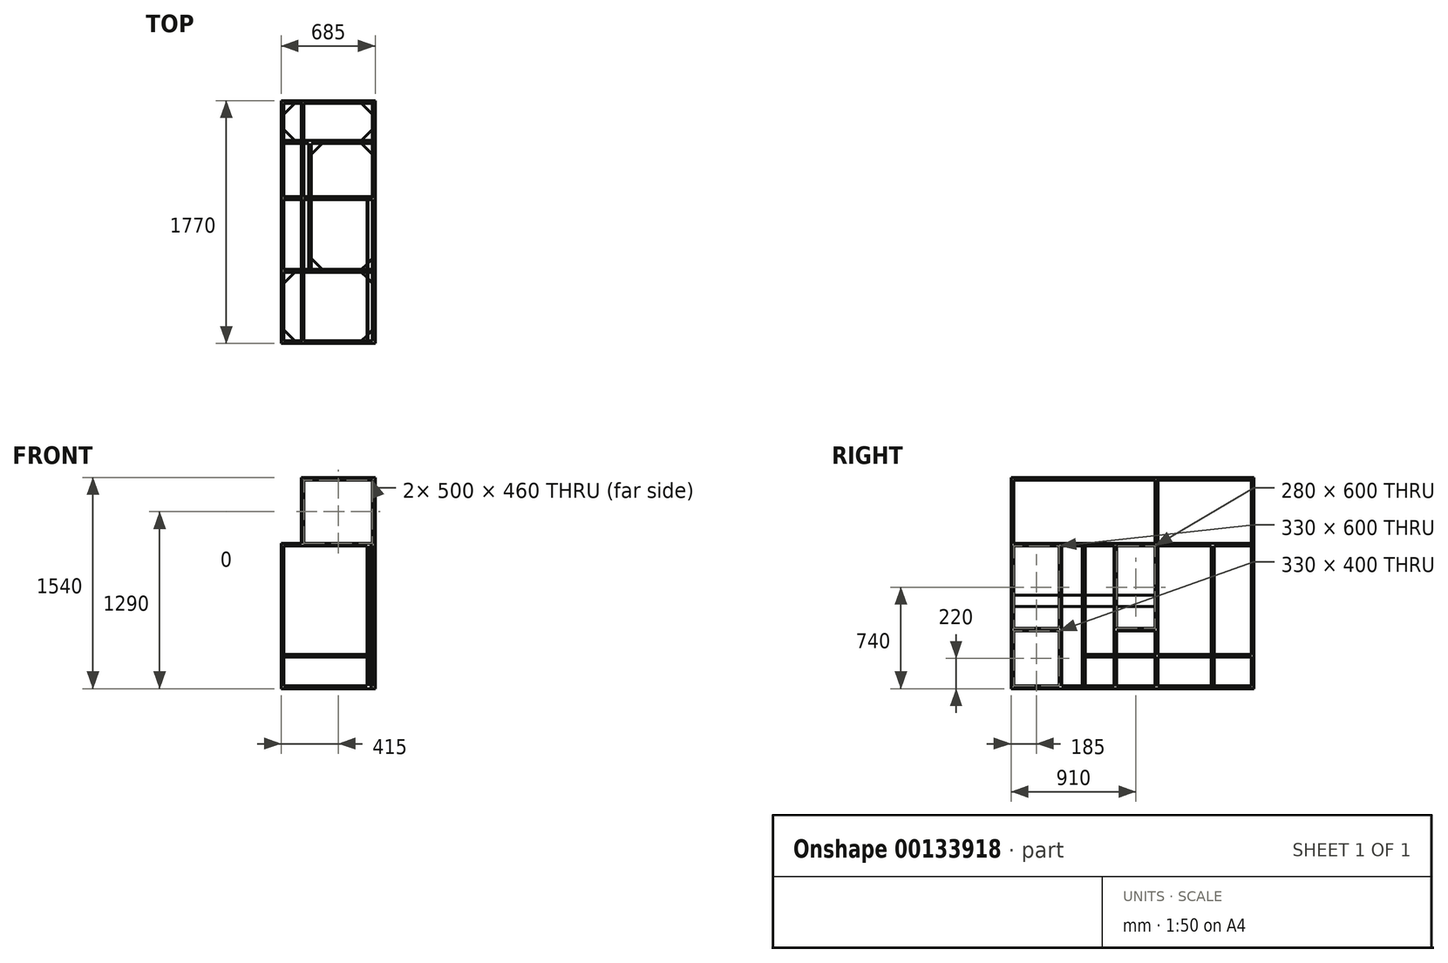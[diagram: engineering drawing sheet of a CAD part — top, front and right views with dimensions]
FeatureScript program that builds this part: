
annotation { "Feature Type Name" : "Feature", "Feature Type Description" : "" }
export const myFeature = defineFeature(function(context is Context, id is Id, definition is map)
    precondition{}
    {
        {
            var Q0;
            Q0=qCreatedBy(makeId("Front.planeOp"),FACE);
            var sketch = newSketch(context, id + "F0", { "sketchPlane" : qUnion([Q0])});
            skLineSegment(sketch, "E0.bottom", {"start": v(0, 0) * mm, "end": v(20, 0) * mm});
            skLineSegment(sketch, "E0.top", {"start": v(0, 20) * mm, "end": v(20, 20) * mm});
            skLineSegment(sketch, "E0.left", {"start": v(0, 0) * mm, "end": v(0, 20) * mm});
            skLineSegment(sketch, "E0.right", {"start": v(20, 0) * mm, "end": v(20, 20) * mm});
            skSolve(sketch);
        }
        {
            var Q0;
            Q0 = qSketchRegion(id + "F0", true);
            extrude(context, id + "F1", {"entities" : qUnion([Q0]), "oppositeDirection" : true, "depth" : 1770 * mm});
        }
        {
            var Q0;
            Q0=makeQuery(id+"F1.opExtrude","SWEPT_FACE",FACE,{"disambiguationData":[OSD([sQuery(id+"F0.wireOp",EDGE,"E0.left")])]});
            var sketch = newSketch(context, id + "F2", { "sketchPlane" : qUnion([Q0])});
            skLineSegment(sketch, "E1.bottom", {"start": v(0, 20) * mm, "end": v(-20, 20) * mm});
            skLineSegment(sketch, "E1.top", {"start": v(0, 0) * mm, "end": v(-20, 0) * mm});
            skLineSegment(sketch, "E1.left", {"start": v(0, 20) * mm, "end": v(0, 0) * mm});
            skLineSegment(sketch, "E1.right", {"start": v(-20, 20) * mm, "end": v(-20, 0) * mm});
            skLineSegment(sketch, "E2.bottom", {"start": v(-1770, 20) * mm, "end": v(-1750, 20) * mm});
            skLineSegment(sketch, "E2.top", {"start": v(-1770, 0) * mm, "end": v(-1750, 0) * mm});
            skLineSegment(sketch, "E2.left", {"start": v(-1770, 20) * mm, "end": v(-1770, 0) * mm});
            skLineSegment(sketch, "E2.right", {"start": v(-1750, 20) * mm, "end": v(-1750, 0) * mm});
            skSolve(sketch);
        }
        {
            var Q0;
            Q0 = qSketchRegion(id + "F2", true);
            extrude(context, id + "F3", {"entities" : qUnion([Q0]), "operationType" : NewBodyOperationType.ADD, "depth" : 665 * mm});
        }
        {
            var Q0;
            Q0=makeQuery(id+"F3.opExtrude","SWEPT_FACE",FACE,{"disambiguationData":[OSD([sQuery(id+"F2.wireOp",EDGE,"E1.right")])]});
            var sketch = newSketch(context, id + "F4", { "sketchPlane" : qUnion([Q0])});
            skLineSegment(sketch, "E3.bottom", {"start": v(665, 20) * mm, "end": v(645, 20) * mm});
            skLineSegment(sketch, "E3.top", {"start": v(665, 0) * mm, "end": v(645, 0) * mm});
            skLineSegment(sketch, "E3.left", {"start": v(665, 20) * mm, "end": v(665, 0) * mm});
            skLineSegment(sketch, "E3.right", {"start": v(645, 20) * mm, "end": v(645, 0) * mm});
            skSolve(sketch);
        }
        {
            var Q0;
            Q0 = qSketchRegion(id + "F4", true);
            extrude(context, id + "F5", {"entities" : qUnion([Q0]), "operationType" : NewBodyOperationType.ADD, "depth" : 520 * mm});
        }
        {
            var Q0;
            Q0=makeQuery(id+"F3.opExtrude","SWEPT_FACE",FACE,{"disambiguationData":[OSD([sQuery(id+"F2.wireOp",EDGE,"E2.right")])]});
            var sketch = newSketch(context, id + "F6", { "sketchPlane" : qUnion([Q0])});
            skLineSegment(sketch, "E4.bottom", {"start": v(-665, 20) * mm, "end": v(-645, 20) * mm});
            skLineSegment(sketch, "E4.top", {"start": v(-665, 0) * mm, "end": v(-645, 0) * mm});
            skLineSegment(sketch, "E4.left", {"start": v(-665, 20) * mm, "end": v(-665, 0) * mm});
            skLineSegment(sketch, "E4.right", {"start": v(-645, 20) * mm, "end": v(-645, 0) * mm});
            skSolve(sketch);
        }
        {
            var Q0;
            Q0 = qSketchRegion(id + "F6", true);
            extrude(context, id + "F7", {"entities" : qUnion([Q0]), "operationType" : NewBodyOperationType.ADD, "depth" : 290 * mm});
        }
        {
            var Q0;
            Q0=makeQuery(id+"F5.opExtrude","SWEPT_FACE",FACE,{"disambiguationData":[OSD([sQuery(id+"F4.wireOp",EDGE,"E3.right")])]});
            var sketch = newSketch(context, id + "F8", { "sketchPlane" : qUnion([Q0])});
            skLineSegment(sketch, "E5.bottom", {"start": v(540, 20) * mm, "end": v(520, 20) * mm});
            skLineSegment(sketch, "E5.top", {"start": v(540, 0) * mm, "end": v(520, 0) * mm});
            skLineSegment(sketch, "E5.left", {"start": v(540, 20) * mm, "end": v(540, 0) * mm});
            skLineSegment(sketch, "E5.right", {"start": v(520, 20) * mm, "end": v(520, 0) * mm});
            skSolve(sketch);
        }
        {
            var Q0;
            Q0 = qSketchRegion(id + "F8", true);
            extrude(context, id + "F9", {"entities" : qUnion([Q0]), "operationType" : NewBodyOperationType.ADD, "endBound" : BoundingType.UP_TO_NEXT, "depth" : 25 * mm});
        }
        {
            var Q0;
            Q0=makeQuery(id+"F7.opExtrude","SWEPT_FACE",FACE,{"disambiguationData":[OSD([sQuery(id+"F6.wireOp",EDGE,"E4.right")])]});
            var sketch = newSketch(context, id + "F10", { "sketchPlane" : qUnion([Q0])});
            skLineSegment(sketch, "E6.bottom", {"start": v(1460, 20) * mm, "end": v(1480, 20) * mm});
            skLineSegment(sketch, "E6.top", {"start": v(1460, 0) * mm, "end": v(1480, 0) * mm});
            skLineSegment(sketch, "E6.left", {"start": v(1460, 20) * mm, "end": v(1460, 0) * mm});
            skLineSegment(sketch, "E6.right", {"start": v(1480, 20) * mm, "end": v(1480, 0) * mm});
            skSolve(sketch);
        }
        {
            var Q0;
            Q0 = qSketchRegion(id + "F10", true);
            extrude(context, id + "F11", {"entities" : qUnion([Q0]), "operationType" : NewBodyOperationType.ADD, "endBound" : BoundingType.UP_TO_NEXT, "depth" : 25 * mm});
        }
        {
            var Q0;
            Q0=makeQuery(id+"F11.boolean.opBoolean","MERGE",FACE,{"derivedFrom":[makeQuery(id+"F7.opExtrude","CAP_FACE",FACE,{"disambiguationData":[OSD([sQuery(id+"F6.wireOp",EDGE,"E4.bottom"),sQuery(id+"F6.wireOp",EDGE,"E4.top"),sQuery(id+"F6.wireOp",EDGE,"E4.left"),sQuery(id+"F6.wireOp",EDGE,"E4.right")])],"isStart":false}),makeQuery(id+"F11.opExtrude","SWEPT_FACE",FACE,{"disambiguationData":[OSD([sQuery(id+"F10.wireOp",EDGE,"E6.left")])]})]});
            var sketch = newSketch(context, id + "F12", { "sketchPlane" : qUnion([Q0])});
            skLineSegment(sketch, "E7.bottom", {"start": v(-465, 20) * mm, "end": v(-445, 20) * mm});
            skLineSegment(sketch, "E7.top", {"start": v(-465, 0) * mm, "end": v(-445, 0) * mm});
            skLineSegment(sketch, "E7.left", {"start": v(-465, 20) * mm, "end": v(-465, 0) * mm});
            skLineSegment(sketch, "E7.right", {"start": v(-445, 20) * mm, "end": v(-445, 0) * mm});
            skSolve(sketch);
        }
        {
            var Q0;
            Q0 = qSketchRegion(id + "F12", true);
            extrude(context, id + "F13", {"entities" : qUnion([Q0]), "operationType" : NewBodyOperationType.ADD, "endBound" : BoundingType.UP_TO_NEXT, "depth" : 25 * mm});
        }
        {
            var Q0;
            Q0=makeQuery(id+"F13.boolean.opBoolean","MERGE",FACE,{"derivedFrom":[makeQuery(id+"F11.boolean.opBoolean","MERGE",FACE,{"derivedFrom":[makeQuery(id+"F9.boolean.opBoolean","MERGE",FACE,{"derivedFrom":[makeQuery(id+"F7.boolean.opBoolean","MERGE",FACE,{"derivedFrom":[makeQuery(id+"F5.boolean.opBoolean","MERGE",FACE,{"derivedFrom":[makeQuery(id+"F3.boolean.opBoolean","MERGE",FACE,{"derivedFrom":[makeQuery(id+"F1.opExtrude","SWEPT_FACE",FACE,{"disambiguationData":[OSD([sQuery(id+"F0.wireOp",EDGE,"E0.top")])]}),makeQuery(id+"F3.opExtrude","SWEPT_FACE",FACE,{"disambiguationData":[OSD([sQuery(id+"F2.wireOp",EDGE,"E1.bottom")])]}),makeQuery(id+"F3.opExtrude","SWEPT_FACE",FACE,{"disambiguationData":[OSD([sQuery(id+"F2.wireOp",EDGE,"E2.bottom")])]})]}),makeQuery(id+"F5.opExtrude","SWEPT_FACE",FACE,{"disambiguationData":[OSD([sQuery(id+"F4.wireOp",EDGE,"E3.bottom")])]})]}),makeQuery(id+"F7.opExtrude","SWEPT_FACE",FACE,{"disambiguationData":[OSD([sQuery(id+"F6.wireOp",EDGE,"E4.bottom")])]})]}),makeQuery(id+"F9.opExtrude","SWEPT_FACE",FACE,{"disambiguationData":[OSD([sQuery(id+"F8.wireOp",EDGE,"E5.bottom")])]})]}),makeQuery(id+"F11.opExtrude","SWEPT_FACE",FACE,{"disambiguationData":[OSD([sQuery(id+"F10.wireOp",EDGE,"E6.bottom")])]})]}),makeQuery(id+"F13.opExtrude","SWEPT_FACE",FACE,{"disambiguationData":[OSD([sQuery(id+"F12.wireOp",EDGE,"E7.bottom")])]})]});
            var sketch = newSketch(context, id + "F14", { "sketchPlane" : qUnion([Q0])});
            skLineSegment(sketch, "E8.bottom", {"start": v(0, 20) * mm, "end": v(20, 20) * mm});
            skLineSegment(sketch, "E8.top", {"start": v(0, 0) * mm, "end": v(20, 0) * mm});
            skLineSegment(sketch, "E8.left", {"start": v(0, 20) * mm, "end": v(0, 0) * mm});
            skLineSegment(sketch, "E8.right", {"start": v(20, 20) * mm, "end": v(20, 0) * mm});
            skLineSegment(sketch, "E9.bottom", {"start": v(-665, 0) * mm, "end": v(-645, 0) * mm});
            skLineSegment(sketch, "E9.top", {"start": v(-665, 20) * mm, "end": v(-645, 20) * mm});
            skLineSegment(sketch, "E9.left", {"start": v(-665, 0) * mm, "end": v(-665, 20) * mm});
            skLineSegment(sketch, "E9.right", {"start": v(-645, 0) * mm, "end": v(-645, 20) * mm});
            skLineSegment(sketch, "E10.bottom", {"start": v(-645, 520) * mm, "end": v(-665, 520) * mm});
            skLineSegment(sketch, "E10.top", {"start": v(-645, 540) * mm, "end": v(-665, 540) * mm});
            skLineSegment(sketch, "E10.left", {"start": v(-645, 520) * mm, "end": v(-645, 540) * mm});
            skLineSegment(sketch, "E10.right", {"start": v(-665, 520) * mm, "end": v(-665, 540) * mm});
            skLineSegment(sketch, "E11.bottom", {"start": v(20, 1770) * mm, "end": v(0, 1770) * mm});
            skLineSegment(sketch, "E11.top", {"start": v(20, 1750) * mm, "end": v(0, 1750) * mm});
            skLineSegment(sketch, "E11.left", {"start": v(20, 1770) * mm, "end": v(20, 1750) * mm});
            skLineSegment(sketch, "E11.right", {"start": v(0, 1770) * mm, "end": v(0, 1750) * mm});
            skLineSegment(sketch, "E12.bottom", {"start": v(-665, 1460) * mm, "end": v(-645, 1460) * mm});
            skLineSegment(sketch, "E12.top", {"start": v(-665, 1480) * mm, "end": v(-645, 1480) * mm});
            skLineSegment(sketch, "E12.left", {"start": v(-665, 1460) * mm, "end": v(-665, 1480) * mm});
            skLineSegment(sketch, "E12.right", {"start": v(-645, 1460) * mm, "end": v(-645, 1480) * mm});
            skLineSegment(sketch, "E13.bottom", {"start": v(-665, 1770) * mm, "end": v(-645, 1770) * mm});
            skLineSegment(sketch, "E13.top", {"start": v(-665, 1750) * mm, "end": v(-645, 1750) * mm});
            skLineSegment(sketch, "E13.left", {"start": v(-665, 1770) * mm, "end": v(-665, 1750) * mm});
            skLineSegment(sketch, "E13.right", {"start": v(-645, 1770) * mm, "end": v(-645, 1750) * mm});
            skLineSegment(sketch, "E14.bottom", {"start": v(0, 1050) * mm, "end": v(20, 1050) * mm});
            skLineSegment(sketch, "E14.top", {"start": v(0, 1070) * mm, "end": v(20, 1070) * mm});
            skLineSegment(sketch, "E14.left", {"start": v(0, 1050) * mm, "end": v(0, 1070) * mm});
            skLineSegment(sketch, "E14.right", {"start": v(20, 1050) * mm, "end": v(20, 1070) * mm});
            skSolve(sketch);
        }
        {
            var Q0;
            Q0 = qSketchRegion(id + "F14", true);
            extrude(context, id + "F15", {"entities" : qUnion([Q0]), "operationType" : NewBodyOperationType.ADD, "depth" : 1040 * mm});
        }
        {
            var Q0;
            {var subQ0=sQuery(id+"F6.wireOp",EDGE,"E4.bottom");var subQ3=sQuery(id+"F6.wireOp",EDGE,"E4.top");var subQ4=sQuery(id+"F6.wireOp",EDGE,"E4.left");Q0=makeQuery(id+"F15.boolean.opBoolean","MERGE",FACE,{"derivedFrom":[makeQuery(id+"F13.boolean.opBoolean","SPLIT",FACE,{"disambiguationData":[TD([makeQuery(id+"F7.opExtrude","SWEPT_FACE",FACE,{"disambiguationData":[OSD([subQ4])]})])],"derivedFrom":makeQuery(id+"F11.boolean.opBoolean","MERGE",FACE,{"derivedFrom":[makeQuery(id+"F7.opExtrude","CAP_FACE",FACE,{"disambiguationData":[OSD([subQ0,subQ3,subQ4,sQuery(id+"F6.wireOp",EDGE,"E4.right")])],"isStart":false}),makeQuery(id+"F11.opExtrude","SWEPT_FACE",FACE,{"disambiguationData":[OSD([sQuery(id+"F10.wireOp",EDGE,"E6.left")])]})]})}),makeQuery(id+"F15.opExtrude","SWEPT_FACE",FACE,{"disambiguationData":[OSD([sQuery(id+"F14.wireOp",EDGE,"E12.bottom")])]})]});}
            var sketch = newSketch(context, id + "F16", { "sketchPlane" : qUnion([Q0])});
            skLineSegment(sketch, "E15.bottom", {"start": v(-665, 250) * mm, "end": v(-645, 250) * mm});
            skLineSegment(sketch, "E15.top", {"start": v(-665, 230) * mm, "end": v(-645, 230) * mm});
            skLineSegment(sketch, "E15.left", {"start": v(-665, 250) * mm, "end": v(-665, 230) * mm});
            skLineSegment(sketch, "E15.right", {"start": v(-645, 250) * mm, "end": v(-645, 230) * mm});
            skSolve(sketch);
        }
        {
            var Q0;
            Q0 = qSketchRegion(id + "F16", true);
            extrude(context, id + "F17", {"entities" : qUnion([Q0]), "operationType" : NewBodyOperationType.ADD, "endBound" : BoundingType.UP_TO_NEXT, "depth" : 25 * mm});
        }
        {
            var Q0;
            Q0=makeQuery(id+"F15.opExtrude","SWEPT_FACE",FACE,{"disambiguationData":[OSD([sQuery(id+"F14.wireOp",EDGE,"E8.bottom")])]});
            var sketch = newSketch(context, id + "F18", { "sketchPlane" : qUnion([Q0])});
            skLineSegment(sketch, "E16.bottom", {"start": v(-20, 1060) * mm, "end": v(0, 1060) * mm});
            skLineSegment(sketch, "E16.top", {"start": v(-20, 1040) * mm, "end": v(0, 1040) * mm});
            skLineSegment(sketch, "E16.left", {"start": v(-20, 1060) * mm, "end": v(-20, 1040) * mm});
            skLineSegment(sketch, "E16.right", {"start": v(0, 1060) * mm, "end": v(0, 1040) * mm});
            skSolve(sketch);
        }
        {
            var Q0;
            Q0 = qSketchRegion(id + "F18", true);
            extrude(context, id + "F19", {"entities" : qUnion([Q0]), "operationType" : NewBodyOperationType.ADD, "endBound" : BoundingType.UP_TO_NEXT, "depth" : 25 * mm});
        }
        {
            var Q0;
            {var subQ2=sQuery(id+"F14.wireOp",EDGE,"E10.top");var subQ5=sQuery(id+"F4.wireOp",EDGE,"E3.left");var subQ6=makeQuery(id+"F5.opExtrude","SWEPT_FACE",FACE,{"disambiguationData":[OSD([subQ5])]});var subQ10=sQuery(id+"F4.wireOp",EDGE,"E3.bottom");var subQ11=sQuery(id+"F4.wireOp",EDGE,"E3.top");Q0=makeQuery(id+"F17.boolean.opBoolean","SPLIT",FACE,{"disambiguationData":[TD([makeQuery(id+"F17.opExtrude","SWEPT_FACE",FACE,{"disambiguationData":[OSD([sQuery(id+"F16.wireOp",EDGE,"E15.bottom")])]})])],"derivedFrom":makeQuery(id+"F15.boolean.opBoolean","MERGE",FACE,{"derivedFrom":[makeQuery(id+"F13.boolean.opBoolean","SPLIT",FACE,{"disambiguationData":[TD([subQ6])],"derivedFrom":makeQuery(id+"F9.boolean.opBoolean","MERGE",FACE,{"derivedFrom":[makeQuery(id+"F5.opExtrude","CAP_FACE",FACE,{"disambiguationData":[OSD([subQ10,subQ11,subQ5,sQuery(id+"F4.wireOp",EDGE,"E3.right")])],"isStart":false}),makeQuery(id+"F9.opExtrude","SWEPT_FACE",FACE,{"disambiguationData":[OSD([sQuery(id+"F8.wireOp",EDGE,"E5.left")])]})]})}),makeQuery(id+"F15.opExtrude","SWEPT_FACE",FACE,{"disambiguationData":[OSD([subQ2])]})]})});}
            var sketch = newSketch(context, id + "F20", { "sketchPlane" : qUnion([Q0])});
            skLineSegment(sketch, "E17.bottom", {"start": v(665, 1060) * mm, "end": v(645, 1060) * mm});
            skLineSegment(sketch, "E17.top", {"start": v(665, 1040) * mm, "end": v(645, 1040) * mm});
            skLineSegment(sketch, "E17.left", {"start": v(665, 1060) * mm, "end": v(665, 1040) * mm});
            skLineSegment(sketch, "E17.right", {"start": v(645, 1060) * mm, "end": v(645, 1040) * mm});
            skSolve(sketch);
        }
        {
            var Q0;
            Q0 = qSketchRegion(id + "F20", true);
            extrude(context, id + "F21", {"entities" : qUnion([Q0]), "operationType" : NewBodyOperationType.ADD, "endBound" : BoundingType.UP_TO_NEXT, "depth" : 25 * mm});
        }
        {
            var Q0;
            {var subQ17=makeQuery(id+"F9.opExtrude","SWEPT_FACE",FACE,{"disambiguationData":[OSD([sQuery(id+"F8.wireOp",EDGE,"E5.left")])]});Q0=makeQuery(id+"F19.boolean.opBoolean","MERGE",FACE,{"derivedFrom":[makeQuery(id+"F15.opExtrude","SWEPT_FACE",FACE,{"disambiguationData":[OSD([sQuery(id+"F14.wireOp",EDGE,"E8.left")])]}),makeQuery(id+"F15.boolean.opBoolean","MERGE",FACE,{"derivedFrom":[makeQuery(id+"F11.boolean.opBoolean","SPLIT",FACE,{"disambiguationData":[TD([subQ17])],"derivedFrom":makeQuery(id+"F9.boolean.opBoolean","SPLIT",FACE,{"disambiguationData":[TD([makeQuery(id+"F3.opExtrude","SWEPT_FACE",FACE,{"disambiguationData":[OSD([sQuery(id+"F2.wireOp",EDGE,"E2.right")])]})])],"derivedFrom":makeQuery(id+"F1.opExtrude","SWEPT_FACE",FACE,{"disambiguationData":[OSD([sQuery(id+"F0.wireOp",EDGE,"E0.left")])]})})}),makeQuery(id+"F15.opExtrude","SWEPT_FACE",FACE,{"disambiguationData":[OSD([sQuery(id+"F14.wireOp",EDGE,"E14.left")])]})]}),makeQuery(id+"F19.opExtrude","SWEPT_FACE",FACE,{"disambiguationData":[OSD([sQuery(id+"F18.wireOp",EDGE,"E16.right")])]})]});}
            var sketch = newSketch(context, id + "F22", { "sketchPlane" : qUnion([Q0])});
            skLineSegment(sketch, "E18.bottom", {"start": v(-1070, 1060) * mm, "end": v(-1050, 1060) * mm});
            skLineSegment(sketch, "E18.top", {"start": v(-1070, 1040) * mm, "end": v(-1050, 1040) * mm});
            skLineSegment(sketch, "E18.left", {"start": v(-1070, 1060) * mm, "end": v(-1070, 1040) * mm});
            skLineSegment(sketch, "E18.right", {"start": v(-1050, 1060) * mm, "end": v(-1050, 1040) * mm});
            skSolve(sketch);
        }
        {
            var Q0;
            Q0 = qSketchRegion(id + "F22", true);
            extrude(context, id + "F23", {"entities" : qUnion([Q0]), "operationType" : NewBodyOperationType.ADD, "endBound" : BoundingType.UP_TO_NEXT, "depth" : 25 * mm});
        }
        {
            var Q0;
            Q0=makeQuery(id+"F23.boolean.opBoolean","MERGE",FACE,{"derivedFrom":[makeQuery(id+"F21.opExtrude","SWEPT_FACE",FACE,{"disambiguationData":[OSD([sQuery(id+"F20.wireOp",EDGE,"E17.top")])]}),makeQuery(id+"F23.opExtrude","SWEPT_FACE",FACE,{"disambiguationData":[OSD([sQuery(id+"F22.wireOp",EDGE,"E18.top")])]})]});
            var sketch = newSketch(context, id + "F24", { "sketchPlane" : qUnion([Q0])});
            skLineSegment(sketch, "E19.bottom", {"start": v(-645, -1050) * mm, "end": v(-665, -1050) * mm});
            skLineSegment(sketch, "E19.top", {"start": v(-645, -1070) * mm, "end": v(-665, -1070) * mm});
            skLineSegment(sketch, "E19.left", {"start": v(-645, -1050) * mm, "end": v(-645, -1070) * mm});
            skLineSegment(sketch, "E19.right", {"start": v(-665, -1050) * mm, "end": v(-665, -1070) * mm});
            skSolve(sketch);
        }
        {
            var Q0;
            Q0 = qSketchRegion(id + "F24", true);
            extrude(context, id + "F25", {"entities" : qUnion([Q0]), "operationType" : NewBodyOperationType.ADD, "endBound" : BoundingType.UP_TO_NEXT, "depth" : 25 * mm});
        }
        {
            var Q0;
            Q0=makeQuery(id+"F15.opExtrude","SWEPT_FACE",FACE,{"disambiguationData":[OSD([sQuery(id+"F14.wireOp",EDGE,"E10.bottom")])]});
            var sketch = newSketch(context, id + "F26", { "sketchPlane" : qUnion([Q0])});
            skLineSegment(sketch, "E20.bottom", {"start": v(-665, 1060) * mm, "end": v(-645, 1060) * mm});
            skLineSegment(sketch, "E20.top", {"start": v(-665, 1040) * mm, "end": v(-645, 1040) * mm});
            skLineSegment(sketch, "E20.left", {"start": v(-665, 1060) * mm, "end": v(-665, 1040) * mm});
            skLineSegment(sketch, "E20.right", {"start": v(-645, 1060) * mm, "end": v(-645, 1040) * mm});
            skSolve(sketch);
        }
        {
            var Q0;
            Q0 = qSketchRegion(id + "F26", true);
            extrude(context, id + "F27", {"entities" : qUnion([Q0]), "operationType" : NewBodyOperationType.ADD, "endBound" : BoundingType.UP_TO_NEXT, "depth" : 25 * mm});
        }
        {
            var Q0;
            Q0=makeQuery(id+"F27.boolean.opBoolean","MERGE",FACE,{"derivedFrom":[makeQuery(id+"F15.opExtrude","SWEPT_FACE",FACE,{"disambiguationData":[OSD([sQuery(id+"F14.wireOp",EDGE,"E9.right")])]}),makeQuery(id+"F25.boolean.opBoolean","MERGE",FACE,{"derivedFrom":[makeQuery(id+"F21.boolean.opBoolean","MERGE",FACE,{"derivedFrom":[makeQuery(id+"F17.boolean.opBoolean","MERGE",FACE,{"derivedFrom":[makeQuery(id+"F15.opExtrude","SWEPT_FACE",FACE,{"disambiguationData":[OSD([sQuery(id+"F14.wireOp",EDGE,"E10.left")])]}),makeQuery(id+"F15.opExtrude","SWEPT_FACE",FACE,{"disambiguationData":[OSD([sQuery(id+"F14.wireOp",EDGE,"E12.right")])]}),makeQuery(id+"F17.opExtrude","SWEPT_FACE",FACE,{"disambiguationData":[OSD([sQuery(id+"F16.wireOp",EDGE,"E15.right")])]})]}),makeQuery(id+"F21.opExtrude","SWEPT_FACE",FACE,{"disambiguationData":[OSD([sQuery(id+"F20.wireOp",EDGE,"E17.right")])]})]}),makeQuery(id+"F25.opExtrude","SWEPT_FACE",FACE,{"disambiguationData":[OSD([sQuery(id+"F24.wireOp",EDGE,"E19.left")])]})]}),makeQuery(id+"F27.opExtrude","SWEPT_FACE",FACE,{"disambiguationData":[OSD([sQuery(id+"F26.wireOp",EDGE,"E20.right")])]})]});
            var sketch = newSketch(context, id + "F28", { "sketchPlane" : qUnion([Q0])});
            skLineSegment(sketch, "E21.bottom", {"start": v(0, 1060) * mm, "end": v(20, 1060) * mm});
            skLineSegment(sketch, "E21.top", {"start": v(0, 1040) * mm, "end": v(20, 1040) * mm});
            skLineSegment(sketch, "E21.left", {"start": v(0, 1060) * mm, "end": v(0, 1040) * mm});
            skLineSegment(sketch, "E21.right", {"start": v(20, 1060) * mm, "end": v(20, 1040) * mm});
            skSolve(sketch);
        }
        {
            var Q0;
            Q0 = qSketchRegion(id + "F28", true);
            extrude(context, id + "F29", {"entities" : qUnion([Q0]), "operationType" : NewBodyOperationType.ADD, "endBound" : BoundingType.UP_TO_NEXT, "depth" : 25 * mm});
        }
        {
            var Q0;
            Q0=makeQuery(id+"F15.opExtrude","SWEPT_FACE",FACE,{"disambiguationData":[OSD([sQuery(id+"F14.wireOp",EDGE,"E12.top")])]});
            var sketch = newSketch(context, id + "F30", { "sketchPlane" : qUnion([Q0])});
            skLineSegment(sketch, "E22.bottom", {"start": v(665, 230) * mm, "end": v(645, 230) * mm});
            skLineSegment(sketch, "E22.top", {"start": v(665, 250) * mm, "end": v(645, 250) * mm});
            skLineSegment(sketch, "E22.left", {"start": v(665, 230) * mm, "end": v(665, 250) * mm});
            skLineSegment(sketch, "E22.right", {"start": v(645, 230) * mm, "end": v(645, 250) * mm});
            skSolve(sketch);
        }
        {
            var Q0;
            Q0 = qSketchRegion(id + "F30", true);
            extrude(context, id + "F31", {"entities" : qUnion([Q0]), "operationType" : NewBodyOperationType.ADD, "endBound" : BoundingType.UP_TO_NEXT, "depth" : 25 * mm});
        }
        {
            var Q0;
            {var subQ0=makeQuery(id+"F25.opExtrude","SWEPT_FACE",FACE,{"disambiguationData":[OSD([sQuery(id+"F24.wireOp",EDGE,"E19.left")])]});var subQ1=makeQuery(id+"F21.opExtrude","SWEPT_FACE",FACE,{"disambiguationData":[OSD([sQuery(id+"F20.wireOp",EDGE,"E17.right")])]});var subQ2=sQuery(id+"F6.wireOp",EDGE,"E4.right");var subQ4=makeQuery(id+"F17.opExtrude","SWEPT_FACE",FACE,{"disambiguationData":[OSD([sQuery(id+"F16.wireOp",EDGE,"E15.right")])]});var subQ8=sQuery(id+"F14.wireOp",EDGE,"E10.left");var subQ9=makeQuery(id+"F15.opExtrude","SWEPT_FACE",FACE,{"disambiguationData":[OSD([subQ8])]});var subQ11=sQuery(id+"F14.wireOp",EDGE,"E12.right");var subQ14=makeQuery(id+"F15.opExtrude","SWEPT_FACE",FACE,{"disambiguationData":[OSD([subQ11])]});var subQ15=sQuery(id+"F14.wireOp",EDGE,"E9.right");var subQ17=makeQuery(id+"F15.opExtrude","SWEPT_FACE",FACE,{"disambiguationData":[OSD([subQ15])]});var subQ19=makeQuery(id+"F27.opExtrude","SWEPT_FACE",FACE,{"disambiguationData":[OSD([sQuery(id+"F26.wireOp",EDGE,"E20.right")])]});Q0=makeQuery(id+"F31.boolean.opBoolean","MERGE",FACE,{"derivedFrom":[makeQuery(id+"F15.opExtrude","SWEPT_FACE",FACE,{"disambiguationData":[OSD([sQuery(id+"F14.wireOp",EDGE,"E13.right")])]}),makeQuery(id+"F29.boolean.opBoolean","SPLIT",FACE,{"disambiguationData":[TD([makeQuery(id+"F7.opExtrude","SWEPT_FACE",FACE,{"disambiguationData":[OSD([subQ2])]})])],"derivedFrom":makeQuery(id+"F27.boolean.opBoolean","MERGE",FACE,{"derivedFrom":[subQ17,makeQuery(id+"F25.boolean.opBoolean","MERGE",FACE,{"derivedFrom":[makeQuery(id+"F21.boolean.opBoolean","MERGE",FACE,{"derivedFrom":[makeQuery(id+"F17.boolean.opBoolean","MERGE",FACE,{"derivedFrom":[subQ9,subQ14,subQ4]}),subQ1]}),subQ0]}),subQ19]})}),makeQuery(id+"F31.opExtrude","SWEPT_FACE",FACE,{"disambiguationData":[OSD([sQuery(id+"F30.wireOp",EDGE,"E22.right")])]})]});}
            var sketch = newSketch(context, id + "F32", { "sketchPlane" : qUnion([Q0])});
            skLineSegment(sketch, "E23.bottom", {"start": v(1750, 250) * mm, "end": v(1770, 250) * mm});
            skLineSegment(sketch, "E23.top", {"start": v(1750, 230) * mm, "end": v(1770, 230) * mm});
            skLineSegment(sketch, "E23.left", {"start": v(1750, 250) * mm, "end": v(1750, 230) * mm});
            skLineSegment(sketch, "E23.right", {"start": v(1770, 250) * mm, "end": v(1770, 230) * mm});
            skLineSegment(sketch, "E24.bottom", {"start": v(1050, 250) * mm, "end": v(1070, 250) * mm});
            skLineSegment(sketch, "E24.top", {"start": v(1050, 230) * mm, "end": v(1070, 230) * mm});
            skLineSegment(sketch, "E24.left", {"start": v(1050, 250) * mm, "end": v(1050, 230) * mm});
            skLineSegment(sketch, "E24.right", {"start": v(1070, 250) * mm, "end": v(1070, 230) * mm});
            skSolve(sketch);
        }
        {
            var Q0;
            Q0 = qSketchRegion(id + "F32", true);
            extrude(context, id + "F33", {"entities" : qUnion([Q0]), "operationType" : NewBodyOperationType.ADD, "endBound" : BoundingType.UP_TO_NEXT, "depth" : 25 * mm});
        }
        {
            var Q0;
            Q0=makeQuery(id+"F33.boolean.opBoolean","MERGE",FACE,{"derivedFrom":[makeQuery(id+"F15.opExtrude","SWEPT_FACE",FACE,{"disambiguationData":[OSD([sQuery(id+"F14.wireOp",EDGE,"E11.top")])]}),makeQuery(id+"F33.opExtrude","SWEPT_FACE",FACE,{"disambiguationData":[OSD([sQuery(id+"F32.wireOp",EDGE,"E23.left")])]})]});
            var sketch = newSketch(context, id + "F34", { "sketchPlane" : qUnion([Q0])});
            skLineSegment(sketch, "E25.bottom", {"start": v(0, 230) * mm, "end": v(20, 230) * mm});
            skLineSegment(sketch, "E25.top", {"start": v(0, 250) * mm, "end": v(20, 250) * mm});
            skLineSegment(sketch, "E25.left", {"start": v(0, 230) * mm, "end": v(0, 250) * mm});
            skLineSegment(sketch, "E25.right", {"start": v(20, 230) * mm, "end": v(20, 250) * mm});
            skSolve(sketch);
        }
        {
            var Q0;
            Q0 = qSketchRegion(id + "F34", true);
            extrude(context, id + "F35", {"entities" : qUnion([Q0]), "operationType" : NewBodyOperationType.ADD, "endBound" : BoundingType.UP_TO_NEXT, "depth" : 25 * mm});
        }
        {
            var Q0;
            {var subQ0=sQuery(id+"F14.wireOp",EDGE,"E13.top");var subQ1=sQuery(id+"F14.wireOp",EDGE,"E12.right");var subQ2=makeQuery(id+"F15.opExtrude","SWEPT_FACE",FACE,{"disambiguationData":[OSD([subQ1])]});var subQ3=sQuery(id+"F14.wireOp",EDGE,"E13.bottom");var subQ4=sQuery(id+"F14.wireOp",EDGE,"E13.right");var subQ5=makeQuery(id+"F25.opExtrude","SWEPT_FACE",FACE,{"disambiguationData":[OSD([sQuery(id+"F24.wireOp",EDGE,"E19.left")])]});var subQ6=sQuery(id+"F0.wireOp",EDGE,"E0.top");var subQ7=makeQuery(id+"F21.opExtrude","SWEPT_FACE",FACE,{"disambiguationData":[OSD([sQuery(id+"F20.wireOp",EDGE,"E17.right")])]});var subQ8=sQuery(id+"F14.wireOp",EDGE,"E10.left");var subQ9=makeQuery(id+"F15.opExtrude","SWEPT_FACE",FACE,{"disambiguationData":[OSD([subQ8])]});var subQ10=sQuery(id+"F14.wireOp",EDGE,"E9.right");var subQ11=makeQuery(id+"F15.opExtrude","SWEPT_FACE",FACE,{"disambiguationData":[OSD([subQ10])]});var subQ12=makeQuery(id+"F15.opExtrude","SWEPT_FACE",FACE,{"disambiguationData":[OSD([subQ4])]});var subQ13=makeQuery(id+"F17.opExtrude","SWEPT_FACE",FACE,{"disambiguationData":[OSD([sQuery(id+"F16.wireOp",EDGE,"E15.right")])]});var subQ14=makeQuery(id+"F27.opExtrude","SWEPT_FACE",FACE,{"disambiguationData":[OSD([sQuery(id+"F26.wireOp",EDGE,"E20.right")])]});var subQ15=makeQuery(id+"F31.opExtrude","SWEPT_FACE",FACE,{"disambiguationData":[OSD([sQuery(id+"F30.wireOp",EDGE,"E22.right")])]});var subQ16=sQuery(id+"F6.wireOp",EDGE,"E4.right");Q0=makeQuery(id+"F33.boolean.opBoolean","SPLIT",FACE,{"disambiguationData":[TD([makeQuery(id+"F1.opExtrude","CAP_FACE",FACE,{"disambiguationData":[OSD([sQuery(id+"F0.wireOp",EDGE,"E0.bottom"),subQ6,sQuery(id+"F0.wireOp",EDGE,"E0.left"),sQuery(id+"F0.wireOp",EDGE,"E0.right")])],"isStart":false}),makeQuery(id+"F3.opExtrude","SWEPT_FACE",FACE,{"disambiguationData":[OSD([sQuery(id+"F2.wireOp",EDGE,"E2.left")])]}),subQ11,subQ9,makeQuery(id+"F15.opExtrude","SWEPT_FACE",FACE,{"disambiguationData":[OSD([sQuery(id+"F14.wireOp",EDGE,"E11.bottom")])]}),makeQuery(id+"F15.opExtrude","SWEPT_FACE",FACE,{"disambiguationData":[OSD([sQuery(id+"F14.wireOp",EDGE,"E11.top")])]}),subQ2,makeQuery(id+"F15.opExtrude","SWEPT_FACE",FACE,{"disambiguationData":[OSD([subQ3])]}),makeQuery(id+"F15.opExtrude","CAP_FACE",FACE,{"disambiguationData":[OSD([subQ3,subQ0,sQuery(id+"F14.wireOp",EDGE,"E13.left"),subQ4])],"isStart":false}),makeQuery(id+"F15.opExtrude","SWEPT_FACE",FACE,{"disambiguationData":[OSD([subQ0])]}),subQ12,subQ13,subQ7,subQ5,subQ14,makeQuery(id+"F31.opExtrude","SWEPT_FACE",FACE,{"disambiguationData":[OSD([sQuery(id+"F30.wireOp",EDGE,"E22.top")])]}),subQ15,makeQuery(id+"F33.opExtrude","SWEPT_FACE",FACE,{"disambiguationData":[OSD([sQuery(id+"F32.wireOp",EDGE,"E23.bottom")])]}),makeQuery(id+"F33.opExtrude","SWEPT_FACE",FACE,{"disambiguationData":[OSD([sQuery(id+"F32.wireOp",EDGE,"E23.left")])]}),makeQuery(id+"F33.opExtrude","SWEPT_FACE",FACE,{"disambiguationData":[OSD([sQuery(id+"F32.wireOp",EDGE,"E23.right")])]})])],"derivedFrom":makeQuery(id+"F31.boolean.opBoolean","MERGE",FACE,{"derivedFrom":[subQ12,makeQuery(id+"F29.boolean.opBoolean","SPLIT",FACE,{"disambiguationData":[TD([makeQuery(id+"F7.opExtrude","SWEPT_FACE",FACE,{"disambiguationData":[OSD([subQ16])]})])],"derivedFrom":makeQuery(id+"F27.boolean.opBoolean","MERGE",FACE,{"derivedFrom":[subQ11,makeQuery(id+"F25.boolean.opBoolean","MERGE",FACE,{"derivedFrom":[makeQuery(id+"F21.boolean.opBoolean","MERGE",FACE,{"derivedFrom":[makeQuery(id+"F17.boolean.opBoolean","MERGE",FACE,{"derivedFrom":[subQ9,subQ2,subQ13]}),subQ7]}),subQ5]}),subQ14]})}),subQ15]})});}
            var sketch = newSketch(context, id + "F36", { "sketchPlane" : qUnion([Q0])});
            skLineSegment(sketch, "E26.bottom", {"start": v(1770, 1060) * mm, "end": v(1750, 1060) * mm});
            skLineSegment(sketch, "E26.top", {"start": v(1770, 1040) * mm, "end": v(1750, 1040) * mm});
            skLineSegment(sketch, "E26.left", {"start": v(1770, 1060) * mm, "end": v(1770, 1040) * mm});
            skLineSegment(sketch, "E26.right", {"start": v(1750, 1060) * mm, "end": v(1750, 1040) * mm});
            skSolve(sketch);
        }
        {
            var Q0;
            Q0 = qSketchRegion(id + "F36", true);
            extrude(context, id + "F37", {"entities" : qUnion([Q0]), "operationType" : NewBodyOperationType.ADD, "endBound" : BoundingType.UP_TO_NEXT, "depth" : 25 * mm});
        }
        {
            var Q0;
            {var subQ3=sQuery(id+"F14.wireOp",EDGE,"E12.top");Q0=makeQuery(id+"F31.boolean.opBoolean","SPLIT",FACE,{"disambiguationData":[TD([makeQuery(id+"F19.opExtrude","SWEPT_FACE",FACE,{"disambiguationData":[OSD([sQuery(id+"F18.wireOp",EDGE,"E16.bottom")])]})])],"derivedFrom":makeQuery(id+"F15.opExtrude","SWEPT_FACE",FACE,{"disambiguationData":[OSD([subQ3])]})});}
            var sketch = newSketch(context, id + "F38", { "sketchPlane" : qUnion([Q0])});
            skLineSegment(sketch, "E27.bottom", {"start": v(645, 1060) * mm, "end": v(665, 1060) * mm});
            skLineSegment(sketch, "E27.top", {"start": v(645, 1040) * mm, "end": v(665, 1040) * mm});
            skLineSegment(sketch, "E27.left", {"start": v(645, 1060) * mm, "end": v(645, 1040) * mm});
            skLineSegment(sketch, "E27.right", {"start": v(665, 1060) * mm, "end": v(665, 1040) * mm});
            skSolve(sketch);
        }
        {
            var Q0;
            Q0 = qSketchRegion(id + "F38", true);
            extrude(context, id + "F39", {"entities" : qUnion([Q0]), "operationType" : NewBodyOperationType.ADD, "endBound" : BoundingType.UP_TO_NEXT, "depth" : 25 * mm});
        }
        {
            var Q0;
            {var subQ0=makeQuery(id+"F7.opExtrude","SWEPT_FACE",FACE,{"disambiguationData":[OSD([sQuery(id+"F6.wireOp",EDGE,"E4.bottom")])]});var subQ1=makeQuery(id+"F5.opExtrude","SWEPT_FACE",FACE,{"disambiguationData":[OSD([sQuery(id+"F4.wireOp",EDGE,"E3.bottom")])]});var subQ2=makeQuery(id+"F13.opExtrude","SWEPT_FACE",FACE,{"disambiguationData":[OSD([sQuery(id+"F12.wireOp",EDGE,"E7.bottom")])]});var subQ3=makeQuery(id+"F3.opExtrude","SWEPT_FACE",FACE,{"disambiguationData":[OSD([sQuery(id+"F2.wireOp",EDGE,"E2.bottom")])]});var subQ5=sQuery(id+"F0.wireOp",EDGE,"E0.top");var subQ6=makeQuery(id+"F3.opExtrude","SWEPT_FACE",FACE,{"disambiguationData":[OSD([sQuery(id+"F2.wireOp",EDGE,"E1.bottom")])]});var subQ7=makeQuery(id+"F11.opExtrude","SWEPT_FACE",FACE,{"disambiguationData":[OSD([sQuery(id+"F10.wireOp",EDGE,"E6.bottom")])]});var subQ8=makeQuery(id+"F1.opExtrude","SWEPT_FACE",FACE,{"disambiguationData":[OSD([subQ5])]});var subQ9=makeQuery(id+"F9.opExtrude","SWEPT_FACE",FACE,{"disambiguationData":[OSD([sQuery(id+"F8.wireOp",EDGE,"E5.bottom")])]});Q0=makeQuery(id+"F15.boolean.opBoolean","SPLIT",FACE,{"disambiguationData":[TD([makeQuery(id+"F3.opExtrude","SWEPT_FACE",FACE,{"disambiguationData":[OSD([sQuery(id+"F2.wireOp",EDGE,"E1.left")])]})])],"derivedFrom":makeQuery(id+"F13.boolean.opBoolean","MERGE",FACE,{"derivedFrom":[makeQuery(id+"F11.boolean.opBoolean","MERGE",FACE,{"derivedFrom":[makeQuery(id+"F9.boolean.opBoolean","MERGE",FACE,{"derivedFrom":[makeQuery(id+"F7.boolean.opBoolean","MERGE",FACE,{"derivedFrom":[makeQuery(id+"F5.boolean.opBoolean","MERGE",FACE,{"derivedFrom":[makeQuery(id+"F3.boolean.opBoolean","MERGE",FACE,{"derivedFrom":[subQ8,subQ6,subQ3]}),subQ1]}),subQ0]}),subQ9]}),subQ7]}),subQ2]})});}
            var sketch = newSketch(context, id + "F40", { "sketchPlane" : qUnion([Q0])});
            skLineSegment(sketch, "E28.bottom", {"start": v(-40, 20) * mm, "end": v(-20, 20) * mm});
            skLineSegment(sketch, "E28.top", {"start": v(-40, 0) * mm, "end": v(-20, 0) * mm});
            skLineSegment(sketch, "E28.left", {"start": v(-40, 20) * mm, "end": v(-40, 0) * mm});
            skLineSegment(sketch, "E28.right", {"start": v(-20, 20) * mm, "end": v(-20, 0) * mm});
            skSolve(sketch);
        }
        {
            var Q0;
            Q0 = qSketchRegion(id + "F40", true);
            extrude(context, id + "F41", {"entities" : qUnion([Q0]), "operationType" : NewBodyOperationType.ADD, "endBound" : BoundingType.UP_TO_NEXT, "depth" : 25 * mm});
        }
        {
            var Q0;
            {var subQ1=makeQuery(id+"F3.opExtrude","SWEPT_FACE",FACE,{"disambiguationData":[OSD([sQuery(id+"F2.wireOp",EDGE,"E2.bottom")])]});var subQ2=sQuery(id+"F6.wireOp",EDGE,"E4.bottom");var subQ3=makeQuery(id+"F7.opExtrude","SWEPT_FACE",FACE,{"disambiguationData":[OSD([subQ2])]});var subQ4=makeQuery(id+"F11.opExtrude","SWEPT_FACE",FACE,{"disambiguationData":[OSD([sQuery(id+"F10.wireOp",EDGE,"E6.bottom")])]});var subQ5=makeQuery(id+"F3.opExtrude","SWEPT_FACE",FACE,{"disambiguationData":[OSD([sQuery(id+"F2.wireOp",EDGE,"E1.bottom")])]});var subQ7=makeQuery(id+"F9.opExtrude","SWEPT_FACE",FACE,{"disambiguationData":[OSD([sQuery(id+"F8.wireOp",EDGE,"E5.bottom")])]});var subQ8=sQuery(id+"F4.wireOp",EDGE,"E3.bottom");var subQ9=makeQuery(id+"F1.opExtrude","SWEPT_FACE",FACE,{"disambiguationData":[OSD([sQuery(id+"F0.wireOp",EDGE,"E0.top")])]});var subQ10=makeQuery(id+"F13.opExtrude","SWEPT_FACE",FACE,{"disambiguationData":[OSD([sQuery(id+"F12.wireOp",EDGE,"E7.bottom")])]});var subQ11=makeQuery(id+"F5.opExtrude","SWEPT_FACE",FACE,{"disambiguationData":[OSD([subQ8])]});Q0=makeQuery(id+"F15.boolean.opBoolean","SPLIT",FACE,{"disambiguationData":[TD([makeQuery(id+"F1.opExtrude","SWEPT_FACE",FACE,{"disambiguationData":[OSD([sQuery(id+"F0.wireOp",EDGE,"E0.right")])]})])],"derivedFrom":makeQuery(id+"F13.boolean.opBoolean","MERGE",FACE,{"derivedFrom":[makeQuery(id+"F11.boolean.opBoolean","MERGE",FACE,{"derivedFrom":[makeQuery(id+"F9.boolean.opBoolean","MERGE",FACE,{"derivedFrom":[makeQuery(id+"F7.boolean.opBoolean","MERGE",FACE,{"derivedFrom":[makeQuery(id+"F5.boolean.opBoolean","MERGE",FACE,{"derivedFrom":[makeQuery(id+"F3.boolean.opBoolean","MERGE",FACE,{"derivedFrom":[subQ9,subQ5,subQ1]}),subQ11]}),subQ3]}),subQ7]}),subQ4]}),subQ10]})});}
            var sketch = newSketch(context, id + "F42", { "sketchPlane" : qUnion([Q0])});
            skLineSegment(sketch, "E29.bottom", {"start": v(-20, 540) * mm, "end": v(-40, 540) * mm});
            skLineSegment(sketch, "E29.top", {"start": v(-20, 520) * mm, "end": v(-40, 520) * mm});
            skLineSegment(sketch, "E29.left", {"start": v(-20, 540) * mm, "end": v(-20, 520) * mm});
            skLineSegment(sketch, "E29.right", {"start": v(-40, 540) * mm, "end": v(-40, 520) * mm});
            skSolve(sketch);
        }
        {
            var Q0;
            {var subQ0=makeQuery(id+"F29.opExtrude","SWEPT_FACE",FACE,{"disambiguationData":[OSD([sQuery(id+"F28.wireOp",EDGE,"E21.bottom")])]});var subQ1=makeQuery(id+"F25.opExtrude","SWEPT_FACE",FACE,{"disambiguationData":[OSD([sQuery(id+"F24.wireOp",EDGE,"E19.left")])]});var subQ2=makeQuery(id+"F23.opExtrude","SWEPT_FACE",FACE,{"disambiguationData":[OSD([sQuery(id+"F22.wireOp",EDGE,"E18.bottom")])]});var subQ3=makeQuery(id+"F21.opExtrude","SWEPT_FACE",FACE,{"disambiguationData":[OSD([sQuery(id+"F20.wireOp",EDGE,"E17.right")])]});var subQ4=makeQuery(id+"F19.opExtrude","SWEPT_FACE",FACE,{"disambiguationData":[OSD([sQuery(id+"F18.wireOp",EDGE,"E16.bottom")])]});var subQ5=makeQuery(id+"F23.opExtrude","SWEPT_FACE",FACE,{"disambiguationData":[OSD([sQuery(id+"F22.wireOp",EDGE,"E18.right")])]});var subQ6=makeQuery(id+"F17.opExtrude","SWEPT_FACE",FACE,{"disambiguationData":[OSD([sQuery(id+"F16.wireOp",EDGE,"E15.right")])]});var subQ7=makeQuery(id+"F21.opExtrude","SWEPT_FACE",FACE,{"disambiguationData":[OSD([sQuery(id+"F20.wireOp",EDGE,"E17.bottom")])]});var subQ8=makeQuery(id+"F17.opExtrude","SWEPT_FACE",FACE,{"disambiguationData":[OSD([sQuery(id+"F16.wireOp",EDGE,"E15.top")])]});var subQ9=makeQuery(id+"F31.opExtrude","SWEPT_FACE",FACE,{"disambiguationData":[OSD([sQuery(id+"F30.wireOp",EDGE,"E22.right")])]});var subQ10=sQuery(id+"F14.wireOp",EDGE,"E14.top");var subQ11=sQuery(id+"F14.wireOp",EDGE,"E14.bottom");var subQ12=makeQuery(id+"F15.opExtrude","CAP_FACE",FACE,{"disambiguationData":[OSD([subQ11,subQ10,sQuery(id+"F14.wireOp",EDGE,"E14.left"),sQuery(id+"F14.wireOp",EDGE,"E14.right")])],"isStart":false});var subQ13=sQuery(id+"F6.wireOp",EDGE,"E4.bottom");var subQ14=makeQuery(id+"F7.opExtrude","SWEPT_FACE",FACE,{"disambiguationData":[OSD([subQ13])]});var subQ15=sQuery(id+"F4.wireOp",EDGE,"E3.right");var subQ16=makeQuery(id+"F5.opExtrude","SWEPT_FACE",FACE,{"disambiguationData":[OSD([subQ15])]});var subQ17=makeQuery(id+"F27.opExtrude","SWEPT_FACE",FACE,{"disambiguationData":[OSD([sQuery(id+"F26.wireOp",EDGE,"E20.right")])]});var subQ18=makeQuery(id+"F27.opExtrude","SWEPT_FACE",FACE,{"disambiguationData":[OSD([sQuery(id+"F26.wireOp",EDGE,"E20.top")])]});var subQ19=makeQuery(id+"F15.opExtrude","SWEPT_FACE",FACE,{"disambiguationData":[OSD([sQuery(id+"F14.wireOp",EDGE,"E13.right")])]});var subQ20=makeQuery(id+"F27.opExtrude","SWEPT_FACE",FACE,{"disambiguationData":[OSD([sQuery(id+"F26.wireOp",EDGE,"E20.bottom")])]});var subQ21=sQuery(id+"F4.wireOp",EDGE,"E3.bottom");var subQ22=makeQuery(id+"F5.opExtrude","CAP_FACE",FACE,{"disambiguationData":[OSD([subQ21,sQuery(id+"F4.wireOp",EDGE,"E3.top"),sQuery(id+"F4.wireOp",EDGE,"E3.left"),subQ15])],"isStart":false});var subQ23=sQuery(id+"F14.wireOp",EDGE,"E12.right");var subQ24=makeQuery(id+"F15.opExtrude","SWEPT_FACE",FACE,{"disambiguationData":[OSD([subQ23])]});var subQ25=makeQuery(id+"F29.opExtrude","SWEPT_FACE",FACE,{"disambiguationData":[OSD([sQuery(id+"F28.wireOp",EDGE,"E21.top")])]});var subQ26=makeQuery(id+"F9.opExtrude","SWEPT_FACE",FACE,{"disambiguationData":[OSD([sQuery(id+"F8.wireOp",EDGE,"E5.right")])]});var subQ27=makeQuery(id+"F25.opExtrude","SWEPT_FACE",FACE,{"disambiguationData":[OSD([sQuery(id+"F24.wireOp",EDGE,"E19.bottom")])]});var subQ28=makeQuery(id+"F1.opExtrude","SWEPT_FACE",FACE,{"disambiguationData":[OSD([sQuery(id+"F0.wireOp",EDGE,"E0.top")])]});var subQ29=makeQuery(id+"F3.opExtrude","SWEPT_FACE",FACE,{"disambiguationData":[OSD([sQuery(id+"F2.wireOp",EDGE,"E1.bottom")])]});var subQ30=makeQuery(id+"F11.opExtrude","SWEPT_FACE",FACE,{"disambiguationData":[OSD([sQuery(id+"F10.wireOp",EDGE,"E6.bottom")])]});var subQ31=makeQuery(id+"F3.opExtrude","SWEPT_FACE",FACE,{"disambiguationData":[OSD([sQuery(id+"F2.wireOp",EDGE,"E2.bottom")])]});var subQ32=makeQuery(id+"F29.opExtrude","SWEPT_FACE",FACE,{"disambiguationData":[OSD([sQuery(id+"F28.wireOp",EDGE,"E21.right")])]});var subQ33=makeQuery(id+"F21.opExtrude","SWEPT_FACE",FACE,{"disambiguationData":[OSD([sQuery(id+"F20.wireOp",EDGE,"E17.top")])]});var subQ34=sQuery(id+"F14.wireOp",EDGE,"E9.right");var subQ35=makeQuery(id+"F15.opExtrude","SWEPT_FACE",FACE,{"disambiguationData":[OSD([subQ34])]});var subQ36=makeQuery(id+"F5.opExtrude","SWEPT_FACE",FACE,{"disambiguationData":[OSD([subQ21])]});var subQ37=sQuery(id+"F14.wireOp",EDGE,"E10.left");var subQ38=sQuery(id+"F14.wireOp",EDGE,"E10.top");var subQ39=sQuery(id+"F14.wireOp",EDGE,"E10.bottom");var subQ40=makeQuery(id+"F15.opExtrude","CAP_FACE",FACE,{"disambiguationData":[OSD([subQ39,subQ38,subQ37,sQuery(id+"F14.wireOp",EDGE,"E10.right")])],"isStart":false});var subQ41=makeQuery(id+"F13.opExtrude","SWEPT_FACE",FACE,{"disambiguationData":[OSD([sQuery(id+"F12.wireOp",EDGE,"E7.bottom")])]});var subQ42=makeQuery(id+"F9.opExtrude","SWEPT_FACE",FACE,{"disambiguationData":[OSD([sQuery(id+"F8.wireOp",EDGE,"E5.left")])]});var subQ43=makeQuery(id+"F15.opExtrude","SWEPT_FACE",FACE,{"disambiguationData":[OSD([subQ39])]});var subQ44=makeQuery(id+"F17.opExtrude","SWEPT_FACE",FACE,{"disambiguationData":[OSD([sQuery(id+"F16.wireOp",EDGE,"E15.bottom")])]});var subQ45=makeQuery(id+"F15.opExtrude","SWEPT_FACE",FACE,{"disambiguationData":[OSD([subQ37])]});var subQ46=sQuery(id+"F14.wireOp",EDGE,"E9.top");var subQ47=makeQuery(id+"F15.opExtrude","CAP_FACE",FACE,{"disambiguationData":[OSD([sQuery(id+"F14.wireOp",EDGE,"E9.bottom"),subQ46,sQuery(id+"F14.wireOp",EDGE,"E9.left"),subQ34])],"isStart":false});var subQ48=makeQuery(id+"F15.opExtrude","SWEPT_FACE",FACE,{"disambiguationData":[OSD([subQ38])]});var subQ49=makeQuery(id+"F15.opExtrude","SWEPT_FACE",FACE,{"disambiguationData":[OSD([subQ46])]});var subQ50=makeQuery(id+"F15.opExtrude","CAP_FACE",FACE,{"disambiguationData":[OSD([sQuery(id+"F14.wireOp",EDGE,"E8.bottom"),sQuery(id+"F14.wireOp",EDGE,"E8.top"),sQuery(id+"F14.wireOp",EDGE,"E8.left"),sQuery(id+"F14.wireOp",EDGE,"E8.right")])],"isStart":false});var subQ51=makeQuery(id+"F23.opExtrude","SWEPT_FACE",FACE,{"disambiguationData":[OSD([sQuery(id+"F22.wireOp",EDGE,"E18.top")])]});var subQ52=makeQuery(id+"F9.opExtrude","SWEPT_FACE",FACE,{"disambiguationData":[OSD([sQuery(id+"F8.wireOp",EDGE,"E5.bottom")])]});var subQ53=sQuery(id+"F14.wireOp",EDGE,"E12.top");var subQ54=sQuery(id+"F14.wireOp",EDGE,"E12.bottom");var subQ55=makeQuery(id+"F15.opExtrude","CAP_FACE",FACE,{"disambiguationData":[OSD([subQ54,subQ53,sQuery(id+"F14.wireOp",EDGE,"E12.left"),subQ23])],"isStart":false});var subQ56=sQuery(id+"F6.wireOp",EDGE,"E4.right");Q0=makeQuery(id+"F33.boolean.opBoolean","SPLIT",FACE,{"disambiguationData":[TD([subQ28,subQ29,subQ31,subQ36,subQ22,subQ16,subQ14,subQ52,subQ42,subQ26,subQ30,subQ41,subQ50,subQ47,subQ49,subQ35,subQ43,subQ40,subQ48,subQ45,subQ55,subQ24,subQ19,makeQuery(id+"F15.opExtrude","SWEPT_FACE",FACE,{"disambiguationData":[OSD([subQ11])]}),subQ12,subQ44,subQ8,subQ6,subQ4,subQ7,subQ33,subQ3,subQ2,subQ51,subQ5,subQ27,subQ1,subQ20,subQ18,subQ17,subQ0,subQ25,subQ32,subQ9,makeQuery(id+"F33.opExtrude","SWEPT_FACE",FACE,{"disambiguationData":[OSD([sQuery(id+"F32.wireOp",EDGE,"E24.bottom")])]}),makeQuery(id+"F33.opExtrude","SWEPT_FACE",FACE,{"disambiguationData":[OSD([sQuery(id+"F32.wireOp",EDGE,"E24.top")])]}),makeQuery(id+"F33.opExtrude","SWEPT_FACE",FACE,{"disambiguationData":[OSD([sQuery(id+"F32.wireOp",EDGE,"E24.left")])]})])],"derivedFrom":makeQuery(id+"F31.boolean.opBoolean","MERGE",FACE,{"derivedFrom":[subQ19,makeQuery(id+"F29.boolean.opBoolean","SPLIT",FACE,{"disambiguationData":[TD([makeQuery(id+"F7.opExtrude","SWEPT_FACE",FACE,{"disambiguationData":[OSD([subQ56])]})])],"derivedFrom":makeQuery(id+"F27.boolean.opBoolean","MERGE",FACE,{"derivedFrom":[subQ35,makeQuery(id+"F25.boolean.opBoolean","MERGE",FACE,{"derivedFrom":[makeQuery(id+"F21.boolean.opBoolean","MERGE",FACE,{"derivedFrom":[makeQuery(id+"F17.boolean.opBoolean","MERGE",FACE,{"derivedFrom":[subQ45,subQ24,subQ6]}),subQ3]}),subQ1]}),subQ17]})}),subQ9]})});}
            var sketch = newSketch(context, id + "F43", { "sketchPlane" : qUnion([Q0])});
            skPoint(sketch, "E30.oppositeSnap0", {"position": v(535, 1060) * mm});
            skLineSegment(sketch, "E30.bottom", {"start": v(540, 1040) * mm, "end": v(520, 1040) * mm});
            skLineSegment(sketch, "E30.top", {"start": v(540, 1060) * mm, "end": v(520, 1060) * mm});
            skLineSegment(sketch, "E30.left", {"start": v(540, 1040) * mm, "end": v(540, 1060) * mm});
            skLineSegment(sketch, "E30.right", {"start": v(520, 1040) * mm, "end": v(520, 1060) * mm});
            skSolve(sketch);
        }
        {
            var Q0;
            Q0 = qSketchRegion(id + "F43", true);
            extrude(context, id + "F44", {"entities" : qUnion([Q0]), "operationType" : NewBodyOperationType.ADD, "endBound" : BoundingType.UP_TO_NEXT, "depth" : 25 * mm});
        }
        {
            var Q0;
            Q0 = qSketchRegion(id + "F42", true);
            extrude(context, id + "F45", {"entities" : qUnion([Q0]), "operationType" : NewBodyOperationType.ADD, "endBound" : BoundingType.UP_TO_NEXT, "depth" : 25 * mm});
        }
        {
            var Q0;
            Q0=makeQuery(id+"F33.opExtrude","SWEPT_FACE",FACE,{"disambiguationData":[OSD([sQuery(id+"F32.wireOp",EDGE,"E24.bottom")])]});
            var sketch = newSketch(context, id + "F46", { "sketchPlane" : qUnion([Q0])});
            skLineSegment(sketch, "E31.bottom", {"start": v(-20, 1070) * mm, "end": v(-40, 1070) * mm});
            skLineSegment(sketch, "E31.top", {"start": v(-20, 1050) * mm, "end": v(-40, 1050) * mm});
            skLineSegment(sketch, "E31.left", {"start": v(-20, 1070) * mm, "end": v(-20, 1050) * mm});
            skLineSegment(sketch, "E31.right", {"start": v(-40, 1070) * mm, "end": v(-40, 1050) * mm});
            skSolve(sketch);
        }
        {
            var Q0;
            Q0 = qSketchRegion(id + "F46", true);
            extrude(context, id + "F47", {"entities" : qUnion([Q0]), "operationType" : NewBodyOperationType.ADD, "endBound" : BoundingType.UP_TO_NEXT, "depth" : 25 * mm});
        }
        {
            var Q0;
            Q0=makeQuery(id+"F25.opExtrude","SWEPT_FACE",FACE,{"disambiguationData":[OSD([sQuery(id+"F24.wireOp",EDGE,"E19.bottom")])]});
            var sketch = newSketch(context, id + "F48", { "sketchPlane" : qUnion([Q0])});
            skLineSegment(sketch, "E32.bottom", {"start": v(-645, 680) * mm, "end": v(-651, 680) * mm});
            skLineSegment(sketch, "E32.top", {"start": v(-645, 600) * mm, "end": v(-651, 600) * mm});
            skLineSegment(sketch, "E32.left", {"start": v(-645, 680) * mm, "end": v(-645, 600) * mm});
            skLineSegment(sketch, "E32.right", {"start": v(-651, 680) * mm, "end": v(-651, 600) * mm});
            skSolve(sketch);
        }
        {
            var Q0;
            Q0 = qSketchRegion(id + "F48", true);
            var Q1;
            Q1=makeQuery(id+"F15.opExtrude","SWEPT_FACE",FACE,{"disambiguationData":[OSD([sQuery(id+"F14.wireOp",EDGE,"E9.top")])]});
            extrude(context, id + "F49", {"entities" : qUnion([Q0]), "operationType" : NewBodyOperationType.ADD, "endBound" : BoundingType.UP_TO_SURFACE, "endBoundEntityFace" : qUnion([Q1]), "depth" : 25 * mm});
        }
        {
            var Q0;
            Q0=makeQuery(id+"F47.boolean.opBoolean","MERGE",FACE,{"derivedFrom":[makeQuery(id+"F23.opExtrude","SWEPT_FACE",FACE,{"disambiguationData":[OSD([sQuery(id+"F22.wireOp",EDGE,"E18.right")])]}),makeQuery(id+"F33.boolean.opBoolean","MERGE",FACE,{"derivedFrom":[makeQuery(id+"F15.opExtrude","SWEPT_FACE",FACE,{"disambiguationData":[OSD([sQuery(id+"F14.wireOp",EDGE,"E14.bottom")])]}),makeQuery(id+"F33.opExtrude","SWEPT_FACE",FACE,{"disambiguationData":[OSD([sQuery(id+"F32.wireOp",EDGE,"E24.left")])]})]}),makeQuery(id+"F47.opExtrude","SWEPT_FACE",FACE,{"disambiguationData":[OSD([sQuery(id+"F46.wireOp",EDGE,"E31.top")])]})]});
            var sketch = newSketch(context, id + "F50", { "sketchPlane" : qUnion([Q0])});
            skLineSegment(sketch, "E33.bottom", {"start": v(-40, 680) * mm, "end": v(-34, 680) * mm});
            skLineSegment(sketch, "E33.top", {"start": v(-40, 600) * mm, "end": v(-34, 600) * mm});
            skLineSegment(sketch, "E33.left", {"start": v(-40, 680) * mm, "end": v(-40, 600) * mm});
            skLineSegment(sketch, "E33.right", {"start": v(-34, 680) * mm, "end": v(-34, 600) * mm});
            skSolve(sketch);
        }
        {
            var Q0;
            Q0 = qSketchRegion(id + "F50", true);
            var Q1;
            Q1=makeQuery(id+"F41.boolean.opBoolean","MERGE",FACE,{"derivedFrom":[makeQuery(id+"F3.opExtrude","SWEPT_FACE",FACE,{"disambiguationData":[OSD([sQuery(id+"F2.wireOp",EDGE,"E1.right")])]}),makeQuery(id+"F29.opExtrude","SWEPT_FACE",FACE,{"disambiguationData":[OSD([sQuery(id+"F28.wireOp",EDGE,"E21.right")])]}),makeQuery(id+"F41.opExtrude","SWEPT_FACE",FACE,{"disambiguationData":[OSD([sQuery(id+"F40.wireOp",EDGE,"E28.bottom")])]})]});
            extrude(context, id + "F51", {"entities" : qUnion([Q0]), "operationType" : NewBodyOperationType.ADD, "endBound" : BoundingType.UP_TO_SURFACE, "endBoundEntityFace" : qUnion([Q1]), "depth" : 25 * mm});
        }
        {
            var Q0;
            Q0=makeQuery(id+"F44.boolean.opBoolean","MERGE",FACE,{"derivedFrom":[makeQuery(id+"F39.boolean.opBoolean","MERGE",FACE,{"derivedFrom":[makeQuery(id+"F29.boolean.opBoolean","MERGE",FACE,{"derivedFrom":[makeQuery(id+"F27.boolean.opBoolean","MERGE",FACE,{"derivedFrom":[makeQuery(id+"F15.opExtrude","CAP_FACE",FACE,{"disambiguationData":[OSD([sQuery(id+"F14.wireOp",EDGE,"E9.bottom"),sQuery(id+"F14.wireOp",EDGE,"E9.top"),sQuery(id+"F14.wireOp",EDGE,"E9.left"),sQuery(id+"F14.wireOp",EDGE,"E9.right")])],"isStart":false}),makeQuery(id+"F23.boolean.opBoolean","MERGE",FACE,{"derivedFrom":[makeQuery(id+"F19.boolean.opBoolean","MERGE",FACE,{"derivedFrom":[makeQuery(id+"F15.opExtrude","CAP_FACE",FACE,{"disambiguationData":[OSD([sQuery(id+"F14.wireOp",EDGE,"E8.bottom"),sQuery(id+"F14.wireOp",EDGE,"E8.top"),sQuery(id+"F14.wireOp",EDGE,"E8.left"),sQuery(id+"F14.wireOp",EDGE,"E8.right")])],"isStart":false}),makeQuery(id+"F15.opExtrude","CAP_FACE",FACE,{"disambiguationData":[OSD([sQuery(id+"F14.wireOp",EDGE,"E14.bottom"),sQuery(id+"F14.wireOp",EDGE,"E14.top"),sQuery(id+"F14.wireOp",EDGE,"E14.left"),sQuery(id+"F14.wireOp",EDGE,"E14.right")])],"isStart":false}),makeQuery(id+"F19.opExtrude","SWEPT_FACE",FACE,{"disambiguationData":[OSD([sQuery(id+"F18.wireOp",EDGE,"E16.bottom")])]})]}),makeQuery(id+"F21.boolean.opBoolean","MERGE",FACE,{"derivedFrom":[makeQuery(id+"F15.opExtrude","CAP_FACE",FACE,{"disambiguationData":[OSD([sQuery(id+"F14.wireOp",EDGE,"E10.bottom"),sQuery(id+"F14.wireOp",EDGE,"E10.top"),sQuery(id+"F14.wireOp",EDGE,"E10.left"),sQuery(id+"F14.wireOp",EDGE,"E10.right")])],"isStart":false}),makeQuery(id+"F15.opExtrude","CAP_FACE",FACE,{"disambiguationData":[OSD([sQuery(id+"F14.wireOp",EDGE,"E12.bottom"),sQuery(id+"F14.wireOp",EDGE,"E12.top"),sQuery(id+"F14.wireOp",EDGE,"E12.left"),sQuery(id+"F14.wireOp",EDGE,"E12.right")])],"isStart":false}),makeQuery(id+"F21.opExtrude","SWEPT_FACE",FACE,{"disambiguationData":[OSD([sQuery(id+"F20.wireOp",EDGE,"E17.bottom")])]})]}),makeQuery(id+"F23.opExtrude","SWEPT_FACE",FACE,{"disambiguationData":[OSD([sQuery(id+"F22.wireOp",EDGE,"E18.bottom")])]})]}),makeQuery(id+"F27.opExtrude","SWEPT_FACE",FACE,{"disambiguationData":[OSD([sQuery(id+"F26.wireOp",EDGE,"E20.bottom")])]})]}),makeQuery(id+"F29.opExtrude","SWEPT_FACE",FACE,{"disambiguationData":[OSD([sQuery(id+"F28.wireOp",EDGE,"E21.bottom")])]})]}),makeQuery(id+"F37.boolean.opBoolean","MERGE",FACE,{"derivedFrom":[makeQuery(id+"F15.opExtrude","CAP_FACE",FACE,{"disambiguationData":[OSD([sQuery(id+"F14.wireOp",EDGE,"E11.bottom"),sQuery(id+"F14.wireOp",EDGE,"E11.top"),sQuery(id+"F14.wireOp",EDGE,"E11.left"),sQuery(id+"F14.wireOp",EDGE,"E11.right")])],"isStart":false}),makeQuery(id+"F15.opExtrude","CAP_FACE",FACE,{"disambiguationData":[OSD([sQuery(id+"F14.wireOp",EDGE,"E13.bottom"),sQuery(id+"F14.wireOp",EDGE,"E13.top"),sQuery(id+"F14.wireOp",EDGE,"E13.left"),sQuery(id+"F14.wireOp",EDGE,"E13.right")])],"isStart":false}),makeQuery(id+"F37.opExtrude","SWEPT_FACE",FACE,{"disambiguationData":[OSD([sQuery(id+"F36.wireOp",EDGE,"E26.bottom")])]})]}),makeQuery(id+"F39.opExtrude","SWEPT_FACE",FACE,{"disambiguationData":[OSD([sQuery(id+"F38.wireOp",EDGE,"E27.bottom")])]})]}),makeQuery(id+"F44.opExtrude","SWEPT_FACE",FACE,{"disambiguationData":[OSD([sQuery(id+"F43.wireOp",EDGE,"E30.top")])]})]});
            var sketch = newSketch(context, id + "F52", { "sketchPlane" : qUnion([Q0])});
            skLineSegment(sketch, "E34.bottom", {"start": v(20, 0) * mm, "end": v(0, 0) * mm});
            skLineSegment(sketch, "E34.top", {"start": v(20, 20) * mm, "end": v(0, 20) * mm});
            skLineSegment(sketch, "E34.left", {"start": v(20, 0) * mm, "end": v(20, 20) * mm});
            skLineSegment(sketch, "E34.right", {"start": v(0, 0) * mm, "end": v(0, 20) * mm});
            skLineSegment(sketch, "E35.bottom", {"start": v(0, 1050) * mm, "end": v(20, 1050) * mm});
            skLineSegment(sketch, "E35.top", {"start": v(0, 1070) * mm, "end": v(20, 1070) * mm});
            skLineSegment(sketch, "E35.left", {"start": v(0, 1050) * mm, "end": v(0, 1070) * mm});
            skLineSegment(sketch, "E35.right", {"start": v(20, 1050) * mm, "end": v(20, 1070) * mm});
            skLineSegment(sketch, "E36.bottom", {"start": v(20, 1750) * mm, "end": v(0, 1750) * mm});
            skLineSegment(sketch, "E36.top", {"start": v(20, 1770) * mm, "end": v(0, 1770) * mm});
            skLineSegment(sketch, "E36.left", {"start": v(20, 1750) * mm, "end": v(20, 1770) * mm});
            skLineSegment(sketch, "E36.right", {"start": v(0, 1750) * mm, "end": v(0, 1770) * mm});
            skLineSegment(sketch, "E37.bottom", {"start": v(-520, 20) * mm, "end": v(-500, 20) * mm});
            skLineSegment(sketch, "E37.top", {"start": v(-520, 0) * mm, "end": v(-500, 0) * mm});
            skLineSegment(sketch, "E37.left", {"start": v(-520, 20) * mm, "end": v(-520, 0) * mm});
            skLineSegment(sketch, "E37.right", {"start": v(-500, 20) * mm, "end": v(-500, 0) * mm});
            skLineSegment(sketch, "E38.bottom", {"start": v(-520, 1050) * mm, "end": v(-500, 1050) * mm});
            skLineSegment(sketch, "E38.top", {"start": v(-520, 1070) * mm, "end": v(-500, 1070) * mm});
            skLineSegment(sketch, "E38.left", {"start": v(-520, 1050) * mm, "end": v(-520, 1070) * mm});
            skLineSegment(sketch, "E38.right", {"start": v(-500, 1050) * mm, "end": v(-500, 1070) * mm});
            skLineSegment(sketch, "E39.bottom", {"start": v(-520, 1750) * mm, "end": v(-500, 1750) * mm});
            skLineSegment(sketch, "E39.top", {"start": v(-520, 1770) * mm, "end": v(-500, 1770) * mm});
            skLineSegment(sketch, "E39.left", {"start": v(-520, 1750) * mm, "end": v(-520, 1770) * mm});
            skLineSegment(sketch, "E39.right", {"start": v(-500, 1750) * mm, "end": v(-500, 1770) * mm});
            skSolve(sketch);
        }
        {
            var Q0;
            Q0 = qSketchRegion(id + "F52", true);
            extrude(context, id + "F53", {"entities" : qUnion([Q0]), "operationType" : NewBodyOperationType.ADD, "depth" : 480 * mm});
        }
        {
            var Q0;
            {var subQ4=sQuery(id+"F14.wireOp",EDGE,"E11.right");var subQ5=sQuery(id+"F14.wireOp",EDGE,"E11.left");var subQ6=sQuery(id+"F14.wireOp",EDGE,"E11.top");var subQ7=makeQuery(id+"F15.opExtrude","CAP_FACE",FACE,{"disambiguationData":[OSD([sQuery(id+"F14.wireOp",EDGE,"E11.bottom"),subQ6,subQ5,subQ4])],"isStart":false});var subQ12=sQuery(id+"F14.wireOp",EDGE,"E13.top");var subQ22=makeQuery(id+"F37.opExtrude","SWEPT_FACE",FACE,{"disambiguationData":[OSD([sQuery(id+"F36.wireOp",EDGE,"E26.right")])]});var subQ23=makeQuery(id+"F15.opExtrude","SWEPT_FACE",FACE,{"disambiguationData":[OSD([subQ12])]});var subQ24=makeQuery(id+"F1.opExtrude","SWEPT_FACE",FACE,{"disambiguationData":[OSD([sQuery(id+"F0.wireOp",EDGE,"E0.right")])]});var subQ33=makeQuery(id+"F15.opExtrude","SWEPT_FACE",FACE,{"disambiguationData":[OSD([subQ6])]});var subQ37=makeQuery(id+"F33.opExtrude","SWEPT_FACE",FACE,{"disambiguationData":[OSD([sQuery(id+"F32.wireOp",EDGE,"E23.left")])]});Q0=makeQuery(id+"F53.boolean.opBoolean","MERGE",FACE,{"derivedFrom":[makeQuery(id+"F39.boolean.opBoolean","SPLIT",FACE,{"disambiguationData":[TD([subQ24])],"derivedFrom":makeQuery(id+"F37.boolean.opBoolean","MERGE",FACE,{"derivedFrom":[makeQuery(id+"F31.boolean.opBoolean","SPLIT",FACE,{"disambiguationData":[TD([makeQuery(id+"F31.opExtrude","SWEPT_FACE",FACE,{"disambiguationData":[OSD([sQuery(id+"F30.wireOp",EDGE,"E22.top")])]})])],"derivedFrom":subQ23}),makeQuery(id+"F35.boolean.opBoolean","SPLIT",FACE,{"disambiguationData":[TD([subQ7])],"derivedFrom":makeQuery(id+"F33.boolean.opBoolean","MERGE",FACE,{"derivedFrom":[subQ33,subQ37]})}),subQ22]})}),makeQuery(id+"F53.opExtrude","SWEPT_FACE",FACE,{"disambiguationData":[OSD([sQuery(id+"F52.wireOp",EDGE,"E36.bottom")])]}),makeQuery(id+"F53.opExtrude","SWEPT_FACE",FACE,{"disambiguationData":[OSD([sQuery(id+"F52.wireOp",EDGE,"E39.bottom")])]})]});}
            var sketch = newSketch(context, id + "F54", { "sketchPlane" : qUnion([Q0])});
            skLineSegment(sketch, "E40.bottom", {"start": v(-520, 1540) * mm, "end": v(-500, 1540) * mm});
            skLineSegment(sketch, "E40.top", {"start": v(-520, 1520) * mm, "end": v(-500, 1520) * mm});
            skLineSegment(sketch, "E40.left", {"start": v(-520, 1540) * mm, "end": v(-520, 1520) * mm});
            skLineSegment(sketch, "E40.right", {"start": v(-500, 1540) * mm, "end": v(-500, 1520) * mm});
            skSolve(sketch);
        }
        {
            var Q0;
            Q0 = qSketchRegion(id + "F54", true);
            var Q1;
            Q1=makeQuery(id+"F53.boolean.opBoolean","MERGE",FACE,{"derivedFrom":[makeQuery(id+"F41.boolean.opBoolean","MERGE",FACE,{"derivedFrom":[makeQuery(id+"F29.boolean.opBoolean","MERGE",FACE,{"derivedFrom":[makeQuery(id+"F15.boolean.opBoolean","MERGE",FACE,{"derivedFrom":[makeQuery(id+"F3.boolean.opBoolean","MERGE",FACE,{"derivedFrom":[makeQuery(id+"F1.opExtrude","CAP_FACE",FACE,{"disambiguationData":[OSD([sQuery(id+"F0.wireOp",EDGE,"E0.bottom"),sQuery(id+"F0.wireOp",EDGE,"E0.top"),sQuery(id+"F0.wireOp",EDGE,"E0.left"),sQuery(id+"F0.wireOp",EDGE,"E0.right")])],"isStart":true}),makeQuery(id+"F3.opExtrude","SWEPT_FACE",FACE,{"disambiguationData":[OSD([sQuery(id+"F2.wireOp",EDGE,"E1.left")])]})]}),makeQuery(id+"F15.opExtrude","SWEPT_FACE",FACE,{"disambiguationData":[OSD([sQuery(id+"F14.wireOp",EDGE,"E8.top")])]}),makeQuery(id+"F15.opExtrude","SWEPT_FACE",FACE,{"disambiguationData":[OSD([sQuery(id+"F14.wireOp",EDGE,"E9.bottom")])]})]}),makeQuery(id+"F29.opExtrude","SWEPT_FACE",FACE,{"disambiguationData":[OSD([sQuery(id+"F28.wireOp",EDGE,"E21.left")])]})]}),makeQuery(id+"F41.opExtrude","SWEPT_FACE",FACE,{"disambiguationData":[OSD([sQuery(id+"F40.wireOp",EDGE,"E28.top")])]})]}),makeQuery(id+"F53.opExtrude","SWEPT_FACE",FACE,{"disambiguationData":[OSD([sQuery(id+"F52.wireOp",EDGE,"E34.bottom")])]}),makeQuery(id+"F53.opExtrude","SWEPT_FACE",FACE,{"disambiguationData":[OSD([sQuery(id+"F52.wireOp",EDGE,"E37.top")])]})]});
            extrude(context, id + "F55", {"entities" : qUnion([Q0]), "operationType" : NewBodyOperationType.ADD, "endBound" : BoundingType.UP_TO_SURFACE, "endBoundEntityFace" : qUnion([Q1]), "depth" : 25 * mm});
        }
        {
            var Q0;
            Q0=makeQuery(id+"F53.opExtrude","SWEPT_FACE",FACE,{"disambiguationData":[OSD([sQuery(id+"F52.wireOp",EDGE,"E35.bottom")])]});
            var sketch = newSketch(context, id + "F56", { "sketchPlane" : qUnion([Q0])});
            skLineSegment(sketch, "E41.bottom", {"start": v(0, 1540) * mm, "end": v(20, 1540) * mm});
            skLineSegment(sketch, "E41.top", {"start": v(0, 1520) * mm, "end": v(20, 1520) * mm});
            skLineSegment(sketch, "E41.left", {"start": v(0, 1540) * mm, "end": v(0, 1520) * mm});
            skLineSegment(sketch, "E41.right", {"start": v(20, 1540) * mm, "end": v(20, 1520) * mm});
            skSolve(sketch);
        }
        {
            var Q0;
            Q0 = qSketchRegion(id + "F56", true);
            extrude(context, id + "F57", {"entities" : qUnion([Q0]), "operationType" : NewBodyOperationType.ADD, "endBound" : BoundingType.UP_TO_NEXT, "depth" : 25 * mm});
        }
        {
            var Q0;
            Q0=makeQuery(id+"F55.boolean.opBoolean","MERGE",FACE,{"derivedFrom":[makeQuery(id+"F53.opExtrude","SWEPT_FACE",FACE,{"disambiguationData":[OSD([sQuery(id+"F52.wireOp",EDGE,"E37.right")])]}),makeQuery(id+"F53.opExtrude","SWEPT_FACE",FACE,{"disambiguationData":[OSD([sQuery(id+"F52.wireOp",EDGE,"E38.right")])]}),makeQuery(id+"F53.opExtrude","SWEPT_FACE",FACE,{"disambiguationData":[OSD([sQuery(id+"F52.wireOp",EDGE,"E39.right")])]}),makeQuery(id+"F55.opExtrude","SWEPT_FACE",FACE,{"disambiguationData":[OSD([sQuery(id+"F54.wireOp",EDGE,"E40.right")])]})]});
            var sketch = newSketch(context, id + "F58", { "sketchPlane" : qUnion([Q0])});
            skLineSegment(sketch, "E42.bottom", {"start": v(0, 1540) * mm, "end": v(20, 1540) * mm});
            skLineSegment(sketch, "E42.top", {"start": v(0, 1520) * mm, "end": v(20, 1520) * mm});
            skLineSegment(sketch, "E42.left", {"start": v(0, 1540) * mm, "end": v(0, 1520) * mm});
            skLineSegment(sketch, "E42.right", {"start": v(20, 1540) * mm, "end": v(20, 1520) * mm});
            skLineSegment(sketch, "E43.bottom", {"start": v(1050, 1520) * mm, "end": v(1070, 1520) * mm});
            skLineSegment(sketch, "E43.top", {"start": v(1050, 1540) * mm, "end": v(1070, 1540) * mm});
            skLineSegment(sketch, "E43.left", {"start": v(1050, 1520) * mm, "end": v(1050, 1540) * mm});
            skLineSegment(sketch, "E43.right", {"start": v(1070, 1520) * mm, "end": v(1070, 1540) * mm});
            skLineSegment(sketch, "E44.bottom", {"start": v(1750, 1520) * mm, "end": v(1770, 1520) * mm});
            skLineSegment(sketch, "E44.top", {"start": v(1750, 1540) * mm, "end": v(1770, 1540) * mm});
            skLineSegment(sketch, "E44.left", {"start": v(1750, 1520) * mm, "end": v(1750, 1540) * mm});
            skLineSegment(sketch, "E44.right", {"start": v(1770, 1520) * mm, "end": v(1770, 1540) * mm});
            skSolve(sketch);
        }
        {
            var Q0;
            Q0 = qSketchRegion(id + "F58", true);
            extrude(context, id + "F59", {"entities" : qUnion([Q0]), "operationType" : NewBodyOperationType.ADD, "endBound" : BoundingType.UP_TO_NEXT, "depth" : 25 * mm});
        }
        {
            var Q0;
            Q0=makeQuery(id+"F13.boolean.opBoolean","MERGE",FACE,{"derivedFrom":[makeQuery(id+"F11.boolean.opBoolean","MERGE",FACE,{"derivedFrom":[makeQuery(id+"F9.boolean.opBoolean","MERGE",FACE,{"derivedFrom":[makeQuery(id+"F7.boolean.opBoolean","MERGE",FACE,{"derivedFrom":[makeQuery(id+"F5.boolean.opBoolean","MERGE",FACE,{"derivedFrom":[makeQuery(id+"F3.boolean.opBoolean","MERGE",FACE,{"derivedFrom":[makeQuery(id+"F1.opExtrude","SWEPT_FACE",FACE,{"disambiguationData":[OSD([sQuery(id+"F0.wireOp",EDGE,"E0.bottom")])]}),makeQuery(id+"F3.opExtrude","SWEPT_FACE",FACE,{"disambiguationData":[OSD([sQuery(id+"F2.wireOp",EDGE,"E1.top")])]}),makeQuery(id+"F3.opExtrude","SWEPT_FACE",FACE,{"disambiguationData":[OSD([sQuery(id+"F2.wireOp",EDGE,"E2.top")])]})]}),makeQuery(id+"F5.opExtrude","SWEPT_FACE",FACE,{"disambiguationData":[OSD([sQuery(id+"F4.wireOp",EDGE,"E3.top")])]})]}),makeQuery(id+"F7.opExtrude","SWEPT_FACE",FACE,{"disambiguationData":[OSD([sQuery(id+"F6.wireOp",EDGE,"E4.top")])]})]}),makeQuery(id+"F9.opExtrude","SWEPT_FACE",FACE,{"disambiguationData":[OSD([sQuery(id+"F8.wireOp",EDGE,"E5.top")])]})]}),makeQuery(id+"F11.opExtrude","SWEPT_FACE",FACE,{"disambiguationData":[OSD([sQuery(id+"F10.wireOp",EDGE,"E6.top")])]})]}),makeQuery(id+"F13.opExtrude","SWEPT_FACE",FACE,{"disambiguationData":[OSD([sQuery(id+"F12.wireOp",EDGE,"E7.top")])]})]});
            var sketch = newSketch(context, id + "F60", { "sketchPlane" : qUnion([Q0])});
            skLineSegment(sketch, "E45", {"start": v(-565, -20) * mm, "end": v(-645, -100) * mm});
            skLineSegment(sketch, "E46", {"start": v(-645, -100) * mm, "end": v(-645, -20) * mm});
            skLineSegment(sketch, "E47", {"start": v(-645, -20) * mm, "end": v(-565, -20) * mm});
            skLineSegment(sketch, "E48", {"start": v(0, -20) * mm, "end": v(-80, -20) * mm});
            skLineSegment(sketch, "E49", {"start": v(-80, -20) * mm, "end": v(0, -100) * mm});
            skLineSegment(sketch, "E50", {"start": v(0, -100) * mm, "end": v(0, -20) * mm});
            skLineSegment(sketch, "E51", {"start": v(-645, -520) * mm, "end": v(-645, -440) * mm});
            skLineSegment(sketch, "E52", {"start": v(-645, -440) * mm, "end": v(-565, -520) * mm});
            skLineSegment(sketch, "E53", {"start": v(-565, -520) * mm, "end": v(-645, -520) * mm});
            skLineSegment(sketch, "E54", {"start": v(0, -440) * mm, "end": v(0, -520) * mm});
            skLineSegment(sketch, "E55", {"start": v(0, -520) * mm, "end": v(-80, -520) * mm});
            skLineSegment(sketch, "E56", {"start": v(-80, -520) * mm, "end": v(0, -440) * mm});
            skLineSegment(sketch, "E57", {"start": v(-80, -540) * mm, "end": v(0, -620) * mm});
            skLineSegment(sketch, "E58", {"start": v(0, -620) * mm, "end": v(0, -540) * mm});
            skLineSegment(sketch, "E59", {"start": v(0, -540) * mm, "end": v(-80, -540) * mm});
            skLineSegment(sketch, "E60", {"start": v(-365, -540) * mm, "end": v(-445, -620) * mm});
            skLineSegment(sketch, "E61", {"start": v(-445, -620) * mm, "end": v(-445, -540) * mm});
            skLineSegment(sketch, "E62", {"start": v(-445, -540) * mm, "end": v(-365, -540) * mm});
            skLineSegment(sketch, "E63", {"start": v(0, -1460) * mm, "end": v(-80, -1460) * mm});
            skLineSegment(sketch, "E64", {"start": v(-80, -1460) * mm, "end": v(0, -1380) * mm});
            skLineSegment(sketch, "E65", {"start": v(0, -1380) * mm, "end": v(0, -1460) * mm});
            skLineSegment(sketch, "E66", {"start": v(-445, -1460) * mm, "end": v(-365, -1460) * mm});
            skLineSegment(sketch, "E67", {"start": v(-365, -1460) * mm, "end": v(-445, -1380) * mm});
            skLineSegment(sketch, "E68", {"start": v(-445, -1380) * mm, "end": v(-445, -1460) * mm});
            skLineSegment(sketch, "E69", {"start": v(0, -1480) * mm, "end": v(-80, -1480) * mm});
            skLineSegment(sketch, "E70", {"start": v(-80, -1480) * mm, "end": v(0, -1560) * mm});
            skLineSegment(sketch, "E71", {"start": v(0, -1560) * mm, "end": v(0, -1480) * mm});
            skLineSegment(sketch, "E72", {"start": v(0, -1750) * mm, "end": v(0, -1670) * mm});
            skLineSegment(sketch, "E73", {"start": v(0, -1670) * mm, "end": v(-80, -1750) * mm});
            skLineSegment(sketch, "E74", {"start": v(-80, -1750) * mm, "end": v(0, -1750) * mm});
            skLineSegment(sketch, "E75", {"start": v(-645, -1750) * mm, "end": v(-565, -1750) * mm});
            skLineSegment(sketch, "E76", {"start": v(-565, -1750) * mm, "end": v(-645, -1670) * mm});
            skLineSegment(sketch, "E77", {"start": v(-645, -1670) * mm, "end": v(-645, -1750) * mm});
            skLineSegment(sketch, "E78", {"start": v(-645, -1560) * mm, "end": v(-565, -1480) * mm});
            skLineSegment(sketch, "E79", {"start": v(-565, -1480) * mm, "end": v(-645, -1480) * mm});
            skLineSegment(sketch, "E80", {"start": v(-645, -1480) * mm, "end": v(-645, -1560) * mm});
            skSolve(sketch);
        }
        {
            var Q0;
            Q0 = qSketchRegion(id + "F60", true);
            extrude(context, id + "F61", {"entities" : qUnion([Q0]), "operationType" : NewBodyOperationType.ADD, "oppositeDirection" : true, "depth" : 6 * mm});
        }
        {
            var Q0;
            {var subQ1=makeQuery(id+"F3.opExtrude","SWEPT_FACE",FACE,{"disambiguationData":[OSD([sQuery(id+"F2.wireOp",EDGE,"E1.right")])]});var subQ4=makeQuery(id+"F9.opExtrude","SWEPT_FACE",FACE,{"disambiguationData":[OSD([sQuery(id+"F8.wireOp",EDGE,"E5.bottom")])]});var subQ9=makeQuery(id+"F11.opExtrude","SWEPT_FACE",FACE,{"disambiguationData":[OSD([sQuery(id+"F10.wireOp",EDGE,"E6.bottom")])]});var subQ11=makeQuery(id+"F3.opExtrude","SWEPT_FACE",FACE,{"disambiguationData":[OSD([sQuery(id+"F2.wireOp",EDGE,"E1.bottom")])]});var subQ12=makeQuery(id+"F1.opExtrude","SWEPT_FACE",FACE,{"disambiguationData":[OSD([sQuery(id+"F0.wireOp",EDGE,"E0.right")])]});var subQ15=makeQuery(id+"F1.opExtrude","SWEPT_FACE",FACE,{"disambiguationData":[OSD([sQuery(id+"F0.wireOp",EDGE,"E0.top")])]});var subQ16=makeQuery(id+"F3.opExtrude","SWEPT_FACE",FACE,{"disambiguationData":[OSD([sQuery(id+"F2.wireOp",EDGE,"E2.bottom")])]});var subQ17=makeQuery(id+"F13.opExtrude","SWEPT_FACE",FACE,{"disambiguationData":[OSD([sQuery(id+"F12.wireOp",EDGE,"E7.bottom")])]});var subQ18=sQuery(id+"F4.wireOp",EDGE,"E3.bottom");var subQ19=makeQuery(id+"F5.opExtrude","SWEPT_FACE",FACE,{"disambiguationData":[OSD([subQ18])]});var subQ20=sQuery(id+"F6.wireOp",EDGE,"E4.bottom");var subQ21=makeQuery(id+"F7.opExtrude","SWEPT_FACE",FACE,{"disambiguationData":[OSD([subQ20])]});Q0=makeQuery(id+"F45.boolean.opBoolean","SPLIT",FACE,{"disambiguationData":[TD([subQ1])],"derivedFrom":makeQuery(id+"F15.boolean.opBoolean","SPLIT",FACE,{"disambiguationData":[TD([subQ12])],"derivedFrom":makeQuery(id+"F13.boolean.opBoolean","MERGE",FACE,{"derivedFrom":[makeQuery(id+"F11.boolean.opBoolean","MERGE",FACE,{"derivedFrom":[makeQuery(id+"F9.boolean.opBoolean","MERGE",FACE,{"derivedFrom":[makeQuery(id+"F7.boolean.opBoolean","MERGE",FACE,{"derivedFrom":[makeQuery(id+"F5.boolean.opBoolean","MERGE",FACE,{"derivedFrom":[makeQuery(id+"F3.boolean.opBoolean","MERGE",FACE,{"derivedFrom":[subQ15,subQ11,subQ16]}),subQ19]}),subQ21]}),subQ4]}),subQ9]}),subQ17]})})});}
            var sketch = newSketch(context, id + "F62", { "sketchPlane" : qUnion([Q0])});
            skLineSegment(sketch, "E81.bottom", {"start": v(0, 350) * mm, "end": v(20, 350) * mm});
            skLineSegment(sketch, "E81.top", {"start": v(0, 370) * mm, "end": v(20, 370) * mm});
            skLineSegment(sketch, "E81.left", {"start": v(0, 350) * mm, "end": v(0, 370) * mm});
            skLineSegment(sketch, "E81.right", {"start": v(20, 350) * mm, "end": v(20, 370) * mm});
            skLineSegment(sketch, "E82.bottom", {"start": v(0, 750) * mm, "end": v(20, 750) * mm});
            skLineSegment(sketch, "E82.top", {"start": v(0, 770) * mm, "end": v(20, 770) * mm});
            skLineSegment(sketch, "E82.left", {"start": v(0, 750) * mm, "end": v(0, 770) * mm});
            skLineSegment(sketch, "E82.right", {"start": v(20, 750) * mm, "end": v(20, 770) * mm});
            skSolve(sketch);
        }
        {
            var Q0;
            Q0 = qSketchRegion(id + "F62", true);
            extrude(context, id + "F63", {"entities" : qUnion([Q0]), "operationType" : NewBodyOperationType.ADD, "endBound" : BoundingType.UP_TO_NEXT, "depth" : 25 * mm});
        }
        {
            var Q0;
            Q0=makeQuery(id+"F15.opExtrude","SWEPT_FACE",FACE,{"disambiguationData":[OSD([sQuery(id+"F14.wireOp",EDGE,"E8.bottom")])]});
            var sketch = newSketch(context, id + "F64", { "sketchPlane" : qUnion([Q0])});
            skLineSegment(sketch, "E83.bottom", {"start": v(-20, 440) * mm, "end": v(0, 440) * mm});
            skLineSegment(sketch, "E83.top", {"start": v(-20, 420) * mm, "end": v(0, 420) * mm});
            skLineSegment(sketch, "E83.left", {"start": v(-20, 440) * mm, "end": v(-20, 420) * mm});
            skLineSegment(sketch, "E83.right", {"start": v(0, 440) * mm, "end": v(0, 420) * mm});
            skSolve(sketch);
        }
        {
            var Q0;
            Q0 = qSketchRegion(id + "F64", true);
            extrude(context, id + "F65", {"entities" : qUnion([Q0]), "operationType" : NewBodyOperationType.ADD, "endBound" : BoundingType.UP_TO_NEXT, "depth" : 25 * mm});
        }
        {
            var Q0;
            Q0=makeQuery(id+"F63.opExtrude","SWEPT_FACE",FACE,{"disambiguationData":[OSD([sQuery(id+"F62.wireOp",EDGE,"E82.top")])]});
            var sketch = newSketch(context, id + "F66", { "sketchPlane" : qUnion([Q0])});
            skLineSegment(sketch, "E84.bottom", {"start": v(-20, 440) * mm, "end": v(0, 440) * mm});
            skLineSegment(sketch, "E84.top", {"start": v(-20, 420) * mm, "end": v(0, 420) * mm});
            skLineSegment(sketch, "E84.left", {"start": v(-20, 440) * mm, "end": v(-20, 420) * mm});
            skLineSegment(sketch, "E84.right", {"start": v(0, 440) * mm, "end": v(0, 420) * mm});
            skSolve(sketch);
        }
        {
            var Q0;
            Q0 = qSketchRegion(id + "F66", true);
            extrude(context, id + "F67", {"entities" : qUnion([Q0]), "operationType" : NewBodyOperationType.ADD, "endBound" : BoundingType.UP_TO_NEXT, "depth" : 25 * mm});
        }
    });
